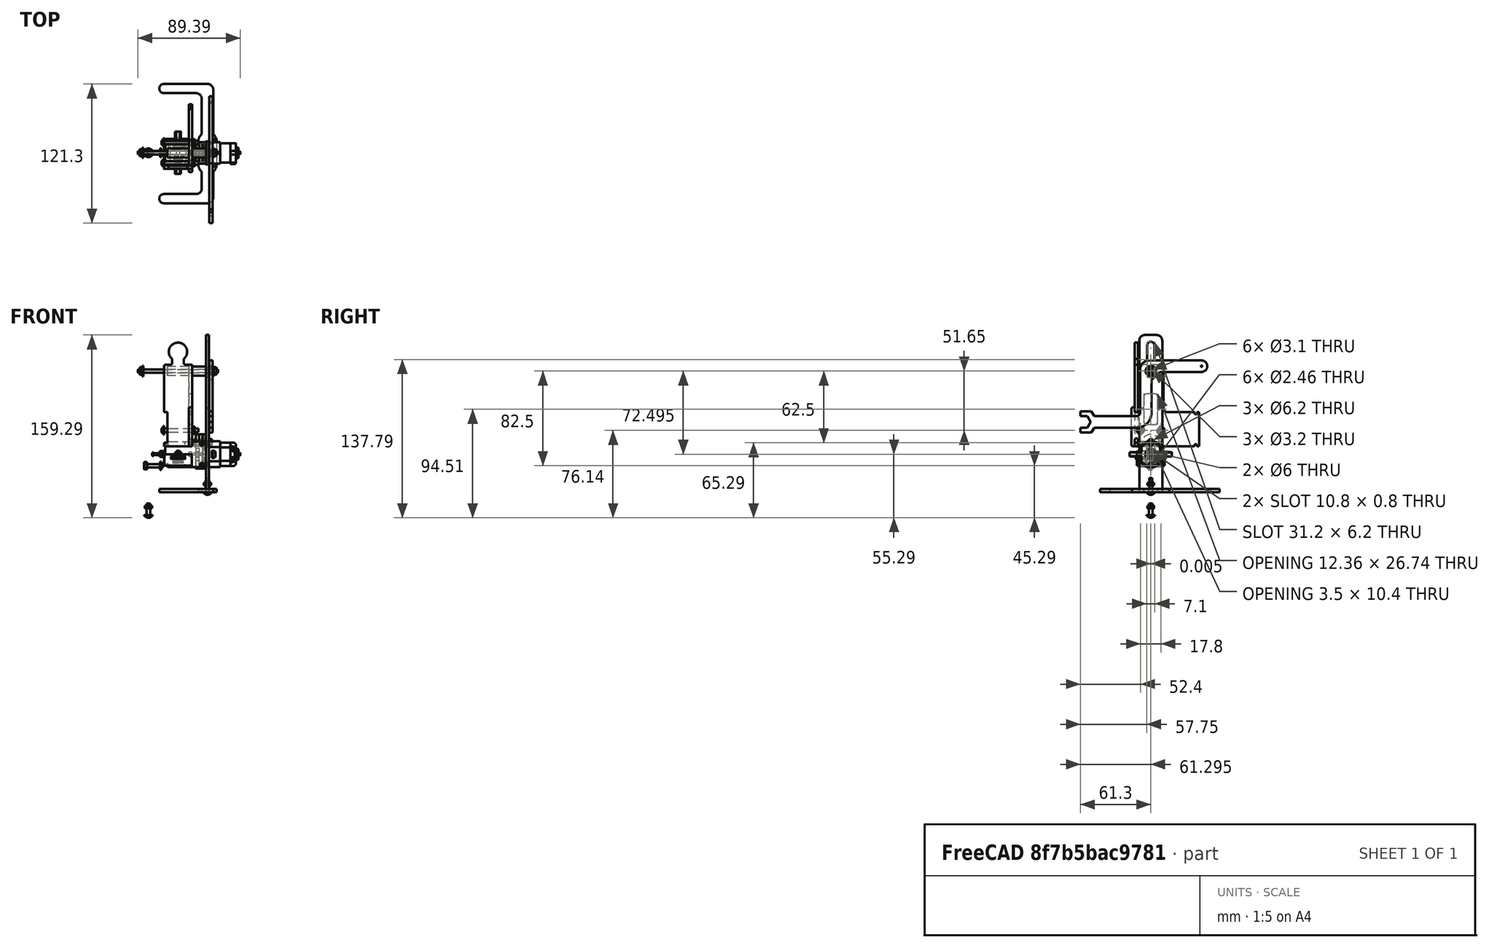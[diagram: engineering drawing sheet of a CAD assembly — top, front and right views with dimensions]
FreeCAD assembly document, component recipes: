
FREECAD ASSEMBLY — COMPONENT RECIPES ("legged_robot_06")

This assembly document has 23 components, labeled P0..P22 below (a component is one placed body or linked part). 21 of them carry a construction recipe — the FreeCAD feature program that regenerates the part from scratch, quoted from this document or its linked companion documents; the rest are supplied as boundary geometry only. No exploded tour is included for this assembly.
COMPONENT P0 — recipe-attached ("cam_right_1", modeled in this document).
Construction recipe (the document's own serialized feature program — sketch geometry with constraints, then the solid features built on it; lengths are millimeters unless a unit is written):

FEATURE [PartDesign::SubShapeBinder] Binder
  BindCopyOnChange = 0
  BindMode = 0
  ClaimChildren = false
  Context = -> Body [Binder.]
  Fuse = false
  MakeFace = true
  OffsetFill = false
  OffsetIntersection = false
  OffsetJoinType = 0
  OffsetOpenResult = false
  PartialLoad = false
  Relative = true
  Support = -> [Part001]
  _Version = 2
FEATURE [Sketcher::SketchObject] Sketch
  ExternalGeometry = -> [Binder]
  FullyConstrained = true
  MapMode = 5
  Placement = pos=(-18.4,0,0) rot=(0.57735,-0.57735,-0.57735;2.0944rad)
  Support = -> [Binder]
  expr: Constraints[38] = Spreadsheet.cam_length
  expr: Constraints[81] = Spreadsheet.angle
  sketch-geometry (37):
    g0: ArcOfCircle CenterX=3.55 CenterY=5 CenterZ=0 NormalX=0 NormalY=0 NormalZ=1 AngleXU=0 Radius=0.4 StartAngle=0 EndAngle=3.14159
    g1: ArcOfCircle CenterX=3.55 CenterY=-5 CenterZ=0 NormalX=0 NormalY=0 NormalZ=1 AngleXU=0 Radius=0.4 StartAngle=3.14159 EndAngle=6.28319
    g2: LineSegment StartX=3.15 StartY=5 StartZ=0 EndX=3.15 EndY=-5 EndZ=0
    g3: LineSegment StartX=3.95 StartY=-5 StartZ=0 EndX=3.95 EndY=5 EndZ=0
    g4: ArcOfCircle CenterX=-3.55 CenterY=5 CenterZ=0 NormalX=0 NormalY=0 NormalZ=1 AngleXU=0 Radius=0.4 StartAngle=3e-16 EndAngle=3.14159
    g5: ArcOfCircle CenterX=-3.55 CenterY=-5 CenterZ=0 NormalX=0 NormalY=0 NormalZ=1 AngleXU=0 Radius=0.4 StartAngle=3.14159 EndAngle=6.28319
    g6: LineSegment StartX=-3.15 StartY=-5 StartZ=0 EndX=-3.15 EndY=5 EndZ=0
    g7: LineSegment StartX=3.55 StartY=5 StartZ=0 EndX=3.55 EndY=-5 EndZ=0
    g8: LineSegment StartX=-3.55 StartY=5 StartZ=0 EndX=-3.55 EndY=-5 EndZ=0
    g9: ArcOfCircle CenterX=1.55 CenterY=5 CenterZ=0 NormalX=0 NormalY=0 NormalZ=1 AngleXU=0 Radius=0.2 StartAngle=0 EndAngle=3.14159
    g10: ArcOfCircle CenterX=1.55 CenterY=-5 CenterZ=0 NormalX=0 NormalY=0 NormalZ=1 AngleXU=0 Radius=0.2 StartAngle=3.14159 EndAngle=6.28319
    g11: LineSegment StartX=1.35 StartY=5 StartZ=0 EndX=1.35 EndY=2.16333 EndZ=0
    g12: LineSegment StartX=1.75 StartY=-5 StartZ=0 EndX=1.75 EndY=5 EndZ=0
    g13: ArcOfCircle CenterX=-1.55 CenterY=5 CenterZ=0 NormalX=0 NormalY=0 NormalZ=1 AngleXU=0 Radius=0.2 StartAngle=5e-16 EndAngle=3.14159
    g14: ArcOfCircle CenterX=-1.55 CenterY=-5 CenterZ=0 NormalX=0 NormalY=0 NormalZ=1 AngleXU=0 Radius=0.2 StartAngle=3.14159 EndAngle=6.28319
    g15: LineSegment StartX=-1.75 StartY=5 StartZ=0 EndX=-1.75 EndY=-5 EndZ=0
    g16: LineSegment StartX=-1.35 StartY=-5 StartZ=0 EndX=-1.35 EndY=-2.16333 EndZ=0
    g17: LineSegment StartX=1.55 StartY=5 StartZ=0 EndX=1.55 EndY=-5 EndZ=0
    g18: LineSegment StartX=-1.55 StartY=5 StartZ=0 EndX=-1.55 EndY=-5 EndZ=0
    g19: LineSegment StartX=3.55 StartY=-4.2e-15 StartZ=0 EndX=1.55 EndY=-3.8e-15 EndZ=0
    g20: ArcOfCircle CenterX=9.6e-15 CenterY=5 CenterZ=0 NormalX=0 NormalY=0 NormalZ=1 AngleXU=0 Radius=7.5 StartAngle=0 EndAngle=3.14159
    g21: ArcOfCircle CenterX=6.9e-15 CenterY=-10 CenterZ=0 NormalX=0 NormalY=0 NormalZ=1 AngleXU=0 Radius=7.5 StartAngle=3.14159 EndAngle=6.28319
    g22: LineSegment StartX=-7.5 StartY=5 StartZ=0 EndX=-7.5 EndY=-10 EndZ=0
    g23: LineSegment StartX=7.5 StartY=-10 StartZ=0 EndX=7.5 EndY=5 EndZ=0
    g24: LineSegment StartX=8.7e-15 StartY=-3.6e-15 StartZ=0 EndX=9.6e-15 EndY=5 EndZ=0
    g25: LineSegment StartX=8.7e-15 StartY=-3.6e-15 StartZ=0 EndX=6.9e-15 EndY=-10 EndZ=0
    g26: Circle CenterX=6.9e-15 CenterY=-10 CenterZ=0 NormalX=0 NormalY=0 NormalZ=1 AngleXU=0 Radius=3.1
    g27: LineSegment StartX=-3.95 StartY=-5 StartZ=0 EndX=-3.95 EndY=5 EndZ=0
    g28: LineSegment StartX=1.55 StartY=-3.8e-15 StartZ=0 EndX=8.7e-15 EndY=-3.6e-15 EndZ=0
    g29: Circle CenterX=8.7e-15 CenterY=-3.6e-15 CenterZ=0 NormalX=0 NormalY=0 NormalZ=1 AngleXU=0 Radius=1.75
    g30: LineSegment StartX=-1.75 StartY=-4.1e-15 StartZ=0 EndX=-1.85 EndY=-4.1e-15 EndZ=0
    g31: LineSegment StartX=-3.55 StartY=-2.9e-15 StartZ=0 EndX=-1.55 EndY=-3.3e-15 EndZ=0
    g32: LineSegment StartX=8.7e-15 StartY=-3.6e-15 StartZ=0 EndX=-1.55 EndY=-3.3e-15 EndZ=0
    g33: LineSegment StartX=-1.35 StartY=2.16333 StartZ=0 EndX=-1.35 EndY=5 EndZ=0
    g34: LineSegment StartX=1.35 StartY=-2.16333 StartZ=0 EndX=1.35 EndY=-5 EndZ=0
    g35: ArcOfCircle CenterX=8.7e-15 CenterY=-3.6e-15 CenterZ=0 NormalX=0 NormalY=0 NormalZ=1 AngleXU=0 Radius=2.55 StartAngle=1.01289 EndAngle=2.1287
    g36: ArcOfCircle CenterX=8.7e-15 CenterY=-3.6e-15 CenterZ=0 NormalX=0 NormalY=0 NormalZ=1 AngleXU=0 Radius=2.55 StartAngle=4.15448 EndAngle=5.2703
  constraints (89):
    c: Tangent(g0,g2) = -1.5708
    c: Tangent(g2,g1) = -1.5708
    c: Tangent(g1,g3) = -1.5708
    c: Tangent(g5,g6) = -1.5708
    c: Tangent(g6,g4) = -1.5708
    c: Radius(g0) = 0.4
    c: Coincident(g7,g0)
    c: Coincident(g7,g1)
    c: Coincident(g8,g4)
    c: Coincident(g8,g5)
    c: Equal(g7,g8)
    c: Distance(g7) = 10
    c: Tangent(g9,g11) = -1.5708
    c: Tangent(g10,g12) = -1.5708
    c: Tangent(g12,g9) = -1.5708
    c: Tangent(g13,g15) = -1.5708
    c: Tangent(g15,g14) = -1.5708
    c: Tangent(g14,g16) = -1.5708
    c: Coincident(g17,g9)
    c: Coincident(g17,g10)
    c: Coincident(g18,g13)
    c: Coincident(g18,g14)
    c: Equal(g17,g7)
    c: Equal(g8,g18)
    c: Symmetric(g10,g9,g19)
    c: Distance(g19) = 2
    c: Perpendicular(g7,g19)
    c: Parallel(g17,g7)
    c: Parallel(g18,g8)
    c: Tangent(g20,g22) = -1.5708
    c: Tangent(g22,g21) = -1.5708
    c: Tangent(g21,g23) = -1.5708
    c: Tangent(g23,g20) = -1.5708
    c: Equal(g20,g21)
    c: Coincident(g24,g20)
    c: Coincident(g25,g21)
    c: Diameter(g20) = 15
    c: Distance(g24) = 5
    c: Distance(g25) = 10
    c: Coincident(g26,g21)
    c: Diameter(g26) = 6.2
    c: Tangent(g27,g4) = 1.5708
    c: Tangent(g27,g5) = 1.5708
    c: Symmetric(g0,g1,g19)
    c: Coincident(g28,g19)
    c: Parallel(g28,g19)
    c: Perpendicular(g28,g24)
    c: Tangent(g0,g3) = -1.5708
    c: PointOnObject(g30,g29)
    c: Horizontal(g30)
    c: Symmetric(g-5,g-5,g30)
    c: DistanceX(g30,g30) = 0.1
    c: Perpendicular(g25,g28)
    c: Symmetric(g14,g13,g31)
    c: Symmetric(g5,g4,g31)
    c: Equal(g31,g19)
    c: Coincident(g32,g31)
    c: Equal(g28,g32)
    c: Perpendicular(g32,g24)
    c: Perpendicular(g32,g18)
    c: Perpendicular(g18,g31)
    c: Tangent(g15,g29)
    c: PointOnObject(g34,g11)
    c: PointOnObject(g33,g-3)
    c: Parallel(g33,g17)
    c: Parallel(g17,g34)
    c: Tangent(g33,g13) = -1.5708
    c: Tangent(g34,g10) = -1.5708
    c: Coincident(g25,g32)
    c: Coincident(g25,g24)
    c: Coincident(g25,g28)
    c: Coincident(g24,g29)
    c: Coincident(g35,g24)
    c: Coincident(g35,g33)
    c: Coincident(g35,g11)
    c: Coincident(g36,g35)
    c: Coincident(g36,g34)
    c: Equal(g36,g-4)
    c: Coincident(g16,g36)
    c: Parallel(g16,g18)
    c: Coincident(g35,g-4)
    c: Angle(g25) = 4.71239
    c: Equal(g5,g1)
    c: Equal(g1,g4)
    c: Equal(g4,g0)
    c: Equal(g13,g9)
    c: Equal(g9,g14)
    c: Equal(g14,g10)
    c: Radius(g9) = 0.2
FEATURE [PartDesign::Pad] Pad
  Direction = (-1,2e-16,-2e-16)
  Length = 2.8
  Length2 = 10
  Profile = -> Sketch
  ReferenceAxis = -> Sketch [N_Axis]
  Reversed = true
  Type = 0
  expr: Length = Spreadsheet.acrylic_thin
FEATURE [PartDesign::Body] Body  label="cam_right_1"
  Group = -> [Sketch,Binder,Pad]
  Origin = -> Origin001
  Tip = -> Pad
COMPONENT P1 — recipe-attached ("leg_right", modeled in this document).
Construction recipe (the document's own serialized feature program — sketch geometry with constraints, then the solid features built on it; lengths are millimeters unless a unit is written):

FEATURE [PartDesign::SubShapeBinder] Binder001
  BindCopyOnChange = 0
  BindMode = 0
  ClaimChildren = false
  Context = -> Body002 [Binder001.]
  Fuse = false
  MakeFace = true
  OffsetFill = false
  OffsetIntersection = false
  OffsetJoinType = 0
  OffsetOpenResult = false
  PartialLoad = false
  Relative = true
  Support = -> [Part001]
  _Version = 2
FEATURE [PartDesign::SubShapeBinder] Binder004
  BindCopyOnChange = 0
  BindMode = 0
  ClaimChildren = false
  Context = -> Body002 [Binder004.]
  Fuse = false
  MakeFace = true
  OffsetFill = false
  OffsetIntersection = false
  OffsetJoinType = 0
  OffsetOpenResult = false
  PartialLoad = false
  Relative = true
  Support = -> [Body004]
  _Version = 2
FEATURE [PartDesign::Plane] DatumPlane003
  AttachmentOffset = pos=(0,0,0.1) rot=(0,0,1;0rad)
  Length = 66.5529
  MapMode = 5
  Placement = pos=(-24.3,-2.7e-15,-2.7e-15) rot=(0.57735,-0.57735,-0.57735;2.0944rad)
  ResizeMode = 0
  Support = -> [Binder004]
  Width = 153.553
FEATURE [Sketcher::SketchObject] Sketch001
  ExternalGeometry = -> [Binder004]
  FullyConstrained = true
  MapMode = 5
  Placement = pos=(-24.3,-2.7e-15,-2.7e-15) rot=(0.57735,-0.57735,-0.57735;2.0944rad)
  Support = -> [DatumPlane003]
  expr: Constraints[117] = Spreadsheet.angle
  expr: Constraints[124] = Spreadsheet.acrylic_thin
  expr: Constraints[50] = Spreadsheet.cam_length
  sketch-geometry (45):
    g0: LineSegment StartX=-10 StartY=84 StartZ=0 EndX=10 EndY=84 EndZ=0
    g1: LineSegment StartX=10 StartY=84 StartZ=0 EndX=10 EndY=-53 EndZ=0
    g2: LineSegment StartX=10 StartY=-53 StartZ=0 EndX=-10 EndY=-53 EndZ=0
    g3: LineSegment StartX=-10 StartY=-53 StartZ=0 EndX=-10 EndY=84 EndZ=0
    g4: LineSegment StartX=1.6 StartY=-9.07624 StartZ=0 EndX=-3.1e-15 EndY=-8.15248 EndZ=0
    g5: LineSegment StartX=-3.1e-15 StartY=-8.15248 StartZ=0 EndX=-1.6 EndY=-9.07624 EndZ=0
    g6: LineSegment StartX=-1.6 StartY=-9.07624 StartZ=0 EndX=-1.6 EndY=-10.9238 EndZ=0
    g7: LineSegment StartX=-1.6 StartY=-10.9238 StartZ=0 EndX=-4.4e-15 EndY=-11.8475 EndZ=0
    g8: LineSegment StartX=-4.4e-15 StartY=-11.8475 StartZ=0 EndX=1.6 EndY=-10.9238 EndZ=0
    g9: LineSegment StartX=1.6 StartY=-10.9238 StartZ=0 EndX=1.6 EndY=-9.07624 EndZ=0
    g10: Circle CenterX=-1.8e-15 CenterY=-10 CenterZ=0 NormalX=0 NormalY=0 NormalZ=1 AngleXU=0 Radius=1.84752
    g11: LineSegment StartX=-1.8e-15 StartY=-10 StartZ=0 EndX=-10 EndY=-10 EndZ=0
    g12: LineSegment StartX=-1.8e-15 StartY=-10 StartZ=0 EndX=10 EndY=-10 EndZ=0
    g13: ArcOfCircle CenterX=8e-16 CenterY=75 CenterZ=0 NormalX=0 NormalY=0 NormalZ=1 AngleXU=0 Radius=3.1 StartAngle=-2.7e-15 EndAngle=3.14159
    g14: ArcOfCircle CenterX=-2e-16 CenterY=50 CenterZ=0 NormalX=0 NormalY=0 NormalZ=1 AngleXU=0 Radius=3.1 StartAngle=3.14159 EndAngle=6.28319
    g15: LineSegment StartX=-3.1 StartY=75 StartZ=0 EndX=-3.1 EndY=50 EndZ=0
    g16: LineSegment StartX=3.1 StartY=50 StartZ=0 EndX=3.1 EndY=75 EndZ=0
    g17: LineSegment StartX=8e-16 StartY=75 StartZ=0 EndX=1.2e-15 EndY=84 EndZ=0
    g18: Circle CenterX=-1.8e-15 CenterY=-10 CenterZ=0 NormalX=0 NormalY=0 NormalZ=1 AngleXU=0 Radius=1.6
    g19: LineSegment StartX=0 StartY=0 StartZ=0 EndX=-1.8e-15 EndY=-10 EndZ=0
    g20: Circle CenterX=0 CenterY=71 CenterZ=0 NormalX=0 NormalY=0 NormalZ=1 AngleXU=0 Radius=3.1
    g21: LineSegment StartX=0 StartY=71 StartZ=0 EndX=0 EndY=0 EndZ=0
    g22: LineSegment StartX=-2e-16 StartY=50 StartZ=0 EndX=3e-16 EndY=62.5 EndZ=0
    g23: LineSegment StartX=8e-16 StartY=75 StartZ=0 EndX=3e-16 EndY=62.5 EndZ=0
    g24: LineSegment StartX=-10 StartY=-53 StartZ=0 EndX=-6 EndY=-53 EndZ=0
    g25: LineSegment StartX=-6 StartY=-53 StartZ=0 EndX=-6 EndY=-50.2 EndZ=0
    g26: LineSegment StartX=-6 StartY=-50.2 StartZ=0 EndX=-1.25 EndY=-50.2 EndZ=0
    g27: LineSegment StartX=-1.25 StartY=-50.2 StartZ=0 EndX=-1.25 EndY=-47.2 EndZ=0
    g28: LineSegment StartX=-1.25 StartY=-47.2 StartZ=0 EndX=-2.75 EndY=-47.2 EndZ=0
    g29: LineSegment StartX=-2.75 StartY=-47.2 StartZ=0 EndX=-2.75 EndY=-44.7 EndZ=0
    g30: LineSegment StartX=-2.75 StartY=-44.7 StartZ=0 EndX=-1.25 EndY=-44.7 EndZ=0
    g31: LineSegment StartX=-1.25 StartY=-44.7 StartZ=0 EndX=-1.25 EndY=-40.7 EndZ=0
    g32: LineSegment StartX=-1.25 StartY=-40.7 StartZ=0 EndX=1.25 EndY=-40.7 EndZ=0
    g33: LineSegment StartX=1.25 StartY=-40.7 StartZ=0 EndX=1.25 EndY=-44.7 EndZ=0
    g34: LineSegment StartX=1.25 StartY=-44.7 StartZ=0 EndX=2.75 EndY=-44.7 EndZ=0
    g35: LineSegment StartX=2.75 StartY=-44.7 StartZ=0 EndX=2.75 EndY=-47.2 EndZ=0
    g36: LineSegment StartX=2.75 StartY=-47.2 StartZ=0 EndX=1.25 EndY=-47.2 EndZ=0
    g37: LineSegment StartX=1.25 StartY=-47.2 StartZ=0 EndX=1.25 EndY=-50.2 EndZ=0
    g38: LineSegment StartX=1.25 StartY=-50.2 StartZ=0 EndX=6 EndY=-50.2 EndZ=0
    g39: LineSegment StartX=6 StartY=-50.2 StartZ=0 EndX=6 EndY=-53 EndZ=0
    g40: LineSegment StartX=6 StartY=-53 StartZ=0 EndX=10 EndY=-53 EndZ=0
    g41: LineSegment StartX=-7 StartY=-10 StartZ=0 EndX=-7 EndY=20 EndZ=0
    g42: LineSegment StartX=7 StartY=20 StartZ=0 EndX=7 EndY=-10 EndZ=0
    g43: Circle CenterX=-7 CenterY=20 CenterZ=0 NormalX=0 NormalY=0 NormalZ=1 AngleXU=0 Radius=0.6
    g44: Circle CenterX=7 CenterY=20 CenterZ=0 NormalX=0 NormalY=0 NormalZ=1 AngleXU=0 Radius=0.6
  constraints (123):
    c: Coincident(g0,g1)
    c: Coincident(g1,g2)
    c: Coincident(g2,g3)
    c: Coincident(g3,g0)
    c: Coincident(g4,g5)
    c: Coincident(g5,g6)
    c: Coincident(g6,g7)
    c: Coincident(g7,g8)
    c: Coincident(g8,g9)
    c: Coincident(g9,g4)
    c: Equal(g4, g5-g9) x5
    c: PointOnObject(g4,g10)
    c: PointOnObject(g5,g10)
    c: PointOnObject(g6,g10)
    c: PointOnObject(g7,g10)
    c: PointOnObject(g8,g10)
    c: PointOnObject(g9,g10)
    c: Distance(g0) = 20
    c: Perpendicular(g3,g0)
    c: Perpendicular(g1,g2)
    c: Perpendicular(g2,g3)
    c: Coincident(g11,g10)
    c: PointOnObject(g11,g3)
    c: Coincident(g12,g10)
    c: PointOnObject(g12,g1)
    c: Perpendicular(g1,g12)
    c: Perpendicular(g3,g11)
    c: Equal(g11,g12)
    c: Distance(g3) = 137
    c: Perpendicular(g11,g6)
    c: Tangent(g13,g15) = -1.5708
    c: Tangent(g15,g14) = -1.5708
    c: Tangent(g14,g16) = -1.5708
    c: Tangent(g16,g13) = -1.5708
    c: Equal(g13,g14)
    c: Diameter(g14) = 6.2
    c: Distance(g13,g14) = 25
    c: Coincident(g17,g13)
    c: Perpendicular(g0,g17)
    c: Distance(g17) = 9
    c: Distance(g10,g14) = 60
    c: Symmetric(g0,g0,g17)
    c: Parallel(g15,g3)
    c: Coincident(g18,g10)
    c: Diameter(g18) = 3.2
    c: Coincident(g19,g10)
    c: Distance(g19) = 10
    c: Coincident(g21,g20)
    c: DistanceY(g21,g21) = 71
    c: Coincident(g21,g19)
    c: Coincident(g22,g14)
    c: Coincident(g23,g13)
    c: Coincident(g23,g22)
    c: Equal(g23,g22)
    c: Parallel(g23,g15)
    c: Tangent(g20,g16)
    c: Vertical(g21)
    c: Coincident(g24,g3)
    c: Coincident(g24,g25)
    c: Coincident(g25,g26)
    c: Coincident(g26,g27)
    c: Coincident(g27,g28)
    c: Coincident(g28,g29)
    c: Coincident(g29,g30)
    c: Coincident(g30,g31)
    c: Coincident(g31,g32)
    c: Coincident(g32,g33)
    c: Coincident(g33,g34)
    c: Coincident(g34,g35)
    c: Coincident(g35,g36)
    c: Coincident(g36,g37)
    c: Coincident(g37,g38)
    c: Coincident(g38,g39)
    c: Coincident(g39,g40)
    c: Coincident(g40,g1)
    c: Perpendicular(g24,g3)
    c: Perpendicular(g40,g1)
    c: Perpendicular(g39,g40)
    c: Perpendicular(g24,g25)
    c: Perpendicular(g26,g25)
    c: Perpendicular(g39,g38)
    c: Perpendicular(g38,g37)
    c: Perpendicular(g26,g27)
    c: Perpendicular(g36,g37)
    c: Perpendicular(g27,g28)
    c: Perpendicular(g35,g36)
    c: Perpendicular(g29,g28)
    c: Perpendicular(g35,g34)
    c: Perpendicular(g30,g29)
    c: Perpendicular(g34,g33)
    c: Perpendicular(g31,g30)
    c: Equal(g25,g39)
    c: Equal(g37,g27)
    c: Equal(g36,g28)
    c: Equal(g30,g34)
    c: Equal(g26,g38)
    c: Distance(g29,g34) = 5.5
    c: Equal(g32,g29)
    c: Equal(g29,g35)
    c: Distance(g31) = 4
    c: Perpendicular(g32,g33)
    c: Equal(g28,g30)
    c: PointOnObject(g41,g11)
    c: Symmetric(g41,g42,g10)
    c: Equal(g41,g42)
    c: Distance(g41,g11) = 3
    c: Coincident(g43,g41)
    c: Coincident(g44,g42)
    c: Equal(g44,g43)
    c: Diameter(g44) = 1.2
    c: Distance(g41) = 30
    c: Perpendicular(g12,g42)
    c: Perpendicular(g11,g41)
    c: Angle(g19) = 4.71239
    c: Equal(g24,g40)
    c: Distance(g24) = 4
    c: DistanceY(g3,g19) = 53
    c: Tangent(g18,g6)
    c: Coincident(g19,g-1)
    c: DistanceY(g29,g29) = 2.5
    c: DistanceY(g25,g25) = 2.8
    c: DistanceY(g27,g27) = 3
    c: Equal(g14,g20)
FEATURE [PartDesign::Pad] Pad004
  Direction = (-1,1e-16,-3e-16)
  Length = 2.8
  Length2 = 10
  Placement = pos=(-24.3,-3e-15,-5e-15) rot=(0.57735,-0.57735,-0.57735;2.0944rad)
  Profile = -> Sketch001
  ReferenceAxis = -> Sketch001 [N_Axis]
  Type = 0
  expr: Length = Spreadsheet.acrylic_thin
FEATURE [PartDesign::Fillet] Fillet
  Base = -> Pad004 [Edge1,Edge2,Edge11,Edge14,Edge53,Edge20,Edge38,Edge35,Edge50,Edge23,Edge41,Edge32,Edge26,Edge47,Edge44,Edge29]
  BaseFeature = -> Pad004
  Placement = pos=(-24.3,-3e-15,-5e-15) rot=(0.57735,-0.57735,-0.57735;2.0944rad)
  Radius = 0.4
  SupportTransform = false
  UseAllEdges = false
FEATURE [PartDesign::Fillet] Fillet001
  Base = -> Fillet [Edge101,Edge103]
  BaseFeature = -> Fillet
  Placement = pos=(-24.3,-3e-15,-5e-15) rot=(0.57735,-0.57735,-0.57735;2.0944rad)
  Radius = 5
  SupportTransform = false
  UseAllEdges = false
FEATURE [PartDesign::Body] Body002  label="leg_right"
  Group = -> [Sketch001,Binder001,Binder004,DatumPlane003,Pad004,Fillet,Fillet001]
  Origin = -> Origin003
  Tip = -> Fillet001
COMPONENT P2 — recipe-attached ("cam_right_2", modeled in this document).
Construction recipe (the document's own serialized feature program — sketch geometry with constraints, then the solid features built on it; lengths are millimeters unless a unit is written):

FEATURE [PartDesign::SubShapeBinder] Binder002
  BindCopyOnChange = 0
  BindMode = 0
  ClaimChildren = false
  Context = -> Body003 [Binder002.]
  Fuse = false
  MakeFace = true
  OffsetFill = false
  OffsetIntersection = false
  OffsetJoinType = 0
  OffsetOpenResult = false
  PartialLoad = false
  Relative = true
  Support = -> [Body]
  _Version = 2
FEATURE [PartDesign::Plane] DatumPlane001
  AttachmentOffset = pos=(0,0,0.1) rot=(0,0,1;0rad)
  Length = 60
  MapMode = 5
  Placement = pos=(-18.5,5.2e-15,-3.9e-15) rot=(-0.57735,0.57735,0.57735;4.18879rad)
  ResizeMode = 0
  Support = -> [Binder002]
  Width = 60
FEATURE [Sketcher::SketchObject] Sketch002
  ExternalGeometry = -> [Binder002]
  FullyConstrained = true
  MapMode = 5
  Placement = pos=(-18.5,5.2e-15,-3.9e-15) rot=(-0.57735,0.57735,0.57735;4.18879rad)
  Support = -> [DatumPlane001]
  sketch-geometry (6):
    g0: ArcOfCircle CenterX=-1.6948e-12 CenterY=5 CenterZ=0 NormalX=0 NormalY=0 NormalZ=1 AngleXU=0 Radius=7.5 StartAngle=2.58e-13 EndAngle=3.14159
    g1: ArcOfCircle CenterX=2.174e-12 CenterY=-10 CenterZ=0 NormalX=0 NormalY=0 NormalZ=1 AngleXU=0 Radius=7.5 StartAngle=3.14159 EndAngle=6.28319
    g2: LineSegment StartX=-7.5 StartY=5 StartZ=0 EndX=-7.5 EndY=-10 EndZ=0
    g3: LineSegment StartX=7.5 StartY=-10 StartZ=0 EndX=7.5 EndY=5 EndZ=0
    g4: Circle CenterX=2.174e-12 CenterY=-10 CenterZ=0 NormalX=0 NormalY=0 NormalZ=1 AngleXU=0 Radius=3.1
    g5: Circle CenterX=0 CenterY=0 CenterZ=0 NormalX=0 NormalY=0 NormalZ=1 AngleXU=0 Radius=1
  constraints (12):
    c: Tangent(g0,g2) = -1.5708
    c: Tangent(g2,g1) = -1.5708
    c: Tangent(g1,g3) = -1.5708
    c: Tangent(g3,g0) = -1.5708
    c: Equal(g0,g1)
    c: Coincident(g0,g-3)
    c: Coincident(g1,g-5)
    c: Equal(g0,g-3)
    c: Coincident(g4,g1)
    c: Equal(g4,g-5)
    c: Coincident(g5,g-6)
    c: Diameter(g5) = 2
FEATURE [PartDesign::Pad] Pad002
  Direction = (-1,2e-16,-2e-16)
  Length = 2.8
  Length2 = 10
  Placement = pos=(-18.5,5e-15,-4e-15) rot=(0.57735,-0.57735,-0.57735;2.0944rad)
  Profile = -> Sketch002
  ReferenceAxis = -> Sketch002 [N_Axis]
  Type = 0
  expr: Length = Spreadsheet.acrylic_thin
FEATURE [PartDesign::Body] Body003  label="cam_right_2"
  Group = -> [Binder002,DatumPlane001,Sketch002,Pad002]
  Origin = -> Origin
  Tip = -> Pad002
COMPONENT P3 — recipe-attached ("cam_right_3", modeled in this document).
Construction recipe (the document's own serialized feature program — sketch geometry with constraints, then the solid features built on it; lengths are millimeters unless a unit is written):

FEATURE [PartDesign::SubShapeBinder] Binder003
  BindCopyOnChange = 0
  BindMode = 0
  ClaimChildren = false
  Context = -> Body004 [Binder003.]
  Fuse = false
  MakeFace = true
  OffsetFill = false
  OffsetIntersection = false
  OffsetJoinType = 0
  OffsetOpenResult = false
  PartialLoad = false
  Relative = true
  Support = -> [Body003]
  _Version = 2
FEATURE [PartDesign::Plane] DatumPlane002
  AttachmentOffset = pos=(0,0,0.1) rot=(0,0,1;0rad)
  Length = 60
  MapMode = 5
  Placement = pos=(-21.4,5.3e-15,-1.05e-14) rot=(-0.57735,0.57735,0.57735;4.18879rad)
  ResizeMode = 0
  Support = -> [Binder003]
  Width = 60
FEATURE [Sketcher::SketchObject] Sketch003
  ExternalGeometry = -> [Binder003]
  FullyConstrained = true
  MapMode = 5
  Placement = pos=(-21.4,5.3e-15,-1.05e-14) rot=(-0.57735,0.57735,0.57735;4.18879rad)
  Support = -> [DatumPlane002]
  sketch-geometry (6):
    g0: ArcOfCircle CenterX=-1.6956e-12 CenterY=5 CenterZ=0 NormalX=0 NormalY=0 NormalZ=1 AngleXU=0 Radius=7.5 StartAngle=2.581e-13 EndAngle=3.14159
    g1: ArcOfCircle CenterX=2.1765e-12 CenterY=-10 CenterZ=0 NormalX=0 NormalY=0 NormalZ=1 AngleXU=0 Radius=7.5 StartAngle=3.14159 EndAngle=6.28319
    g2: LineSegment StartX=-7.5 StartY=5 StartZ=0 EndX=-7.5 EndY=-10 EndZ=0
    g3: LineSegment StartX=7.5 StartY=-10 StartZ=0 EndX=7.5 EndY=5 EndZ=0
    g4: Circle CenterX=2.1765e-12 CenterY=-10 CenterZ=0 NormalX=0 NormalY=0 NormalZ=1 AngleXU=0 Radius=3.1
    g5: Circle CenterX=0 CenterY=0 CenterZ=0 NormalX=0 NormalY=0 NormalZ=1 AngleXU=0 Radius=3
  constraints (12):
    c: Tangent(g0,g2) = -1.5708
    c: Tangent(g2,g1) = -1.5708
    c: Tangent(g1,g3) = -1.5708
    c: Tangent(g3,g0) = -1.5708
    c: Equal(g0,g1)
    c: Coincident(g0,g-3)
    c: Coincident(g1,g-5)
    c: Equal(g0,g-3)
    c: Coincident(g4,g1)
    c: Equal(g4,g-5)
    c: Coincident(g5,g-6)
    c: Diameter(g5) = 6
FEATURE [PartDesign::Pad] Pad003
  Direction = (-1,0,0)
  Length = 2.8
  Length2 = 10
  Placement = pos=(-21.4,1e-15,-2e-15) rot=(0.57735,-0.57735,-0.57735;2.0944rad)
  Profile = -> Sketch003
  ReferenceAxis = -> Sketch003 [N_Axis]
  Type = 0
  expr: Length = Spreadsheet.acrylic_thin
FEATURE [PartDesign::Body] Body004  label="cam_right_3"
  Group = -> [Binder003,DatumPlane002,Sketch003,Pad003]
  Origin = -> Origin005
  Tip = -> Pad003
COMPONENT P4 — recipe-attached ("spacer_right", modeled in this document).
Construction recipe (the document's own serialized feature program — sketch geometry with constraints, then the solid features built on it; lengths are millimeters unless a unit is written):

FEATURE [PartDesign::SubShapeBinder] Binder005
  BindCopyOnChange = 0
  BindMode = 0
  ClaimChildren = false
  Context = -> Body005 [Binder005.]
  Fuse = false
  MakeFace = true
  OffsetFill = false
  OffsetIntersection = false
  OffsetJoinType = 0
  OffsetOpenResult = false
  PartialLoad = false
  Relative = true
  Support = -> [Body004]
  _Version = 2
FEATURE [PartDesign::SubShapeBinder] Binder008
  BindCopyOnChange = 0
  BindMode = 0
  ClaimChildren = false
  Context = -> Body005 [Binder008.]
  Fuse = false
  MakeFace = true
  OffsetFill = false
  OffsetIntersection = false
  OffsetJoinType = 0
  OffsetOpenResult = false
  PartialLoad = false
  Relative = true
  Support = -> [Body002[Pad004.]]
  _Version = 2
FEATURE [Sketcher::SketchObject] Sketch004
  ExternalGeometry = -> [Binder005]
  FullyConstrained = true
  MapMode = 5
  Placement = pos=(-24.3,6.3e-15,-8e-15) rot=(0.57735,0.57735,0.57735;2.0944rad)
  Support = -> [Binder008]
  sketch-geometry (2):
    g0: Circle CenterX=-2.1858e-12 CenterY=-10 CenterZ=0 NormalX=0 NormalY=0 NormalZ=1 AngleXU=0 Radius=3
    g1: Circle CenterX=-2.1858e-12 CenterY=-10 CenterZ=0 NormalX=0 NormalY=0 NormalZ=1 AngleXU=0 Radius=1.6
  constraints (4):
    c: Diameter(g1) = 3.2
    c: Diameter(g0) = 6
    c: Coincident(g1,g-3)
    c: Coincident(g0,g1)
FEATURE [PartDesign::Pad] Pad005
  Direction = (1,-1e-16,4e-16)
  Length = 8.8
  Length2 = 10
  Profile = -> Sketch004
  ReferenceAxis = -> Sketch004 [N_Axis]
  Type = 0
FEATURE [PartDesign::Body] Body005  label="spacer_right"
  Group = -> [Binder005,Sketch004,Pad005,Binder008]
  Origin = -> Origin006
  Tip = -> Pad005
COMPONENT P5 — recipe-attached ("feet_right", modeled in this document).
Construction recipe (the document's own serialized feature program — sketch geometry with constraints, then the solid features built on it; lengths are millimeters unless a unit is written):

FEATURE [PartDesign::SubShapeBinder] Binder009
  BindCopyOnChange = 0
  BindMode = 0
  ClaimChildren = false
  Context = -> Body007 [Binder009.]
  Fuse = false
  MakeFace = true
  OffsetFill = false
  OffsetIntersection = false
  OffsetJoinType = 0
  OffsetOpenResult = false
  PartialLoad = false
  Relative = true
  Support = -> [Body002[Pad004.]]
  _Version = 2
FEATURE [PartDesign::Plane] DatumPlane
  Length = 74.3266
  MapMode = 5
  Placement = pos=(-5.8e-15,-1.75e-14,-53) rot=(1,0,0;3.14159rad)
  ResizeMode = 0
  Support = -> [Binder009]
  Width = 119.627
FEATURE [Sketcher::SketchObject] Sketch006
  ExternalGeometry = -> [Binder009]
  FullyConstrained = true
  MapMode = 5
  Placement = pos=(-5.8e-15,-1.75e-14,-53) rot=(0,0,1;3.14159rad)
  Support = -> [DatumPlane]
  sketch-geometry (51):
    g0: LineSegment StartX=-12.3 StartY=40 StartZ=0 EndX=25.7 EndY=40 EndZ=0
    g1: LineSegment StartX=25.7 StartY=40 StartZ=0 EndX=25.7 EndY=0 EndZ=0
    g2: LineSegment StartX=25.7 StartY=0 StartZ=0 EndX=25.7 EndY=-56 EndZ=0
    g3: LineSegment StartX=25.7 StartY=-56 StartZ=0 EndX=-12.3 EndY=-56 EndZ=0
    g4: ArcOfCircle CenterX=-12.3 CenterY=40 CenterZ=0 NormalX=0 NormalY=0 NormalZ=1 AngleXU=0 Radius=4 StartAngle=1.5708 EndAngle=4.71239
    g5: ArcOfCircle CenterX=-12.3 CenterY=-56 CenterZ=0 NormalX=0 NormalY=0 NormalZ=1 AngleXU=0 Radius=4 StartAngle=1.5708 EndAngle=4.71239
    g6: LineSegment StartX=-12.3 StartY=44 StartZ=0 EndX=25.7 EndY=44 EndZ=0
    g7: LineSegment StartX=-12.3 StartY=36 StartZ=0 EndX=15.7 EndY=36 EndZ=0
    g8: LineSegment StartX=-12.3 StartY=-52 StartZ=0 EndX=15.7 EndY=-52 EndZ=0
    g9: LineSegment StartX=-12.3 StartY=-60 StartZ=0 EndX=25.7 EndY=-60 EndZ=0
    g10: ArcOfCircle CenterX=25.7 CenterY=10.1 CenterZ=0 NormalX=0 NormalY=0 NormalZ=1 AngleXU=0 Radius=8 StartAngle=0 EndAngle=0.895665
    g11: ArcOfCircle CenterX=25.7 CenterY=-9.9 CenterZ=0 NormalX=0 NormalY=0 NormalZ=1 AngleXU=0 Radius=8 StartAngle=3.14159 EndAngle=4.03726
    g12: LineSegment StartX=17.7 StartY=10.1 StartZ=0 EndX=17.7 EndY=-9.9 EndZ=0
    g13: LineSegment StartX=33.7 StartY=-9.9 StartZ=0 EndX=33.7 EndY=10.1 EndZ=0
    g14: LineSegment StartX=20.7 StartY=31 StartZ=0 EndX=20.7 EndY=16.345 EndZ=0
    g15: LineSegment StartX=30.7 StartY=16.345 StartZ=0 EndX=30.7 EndY=39 EndZ=0
    g16: ArcOfCircle CenterX=25.7 CenterY=39 CenterZ=0 NormalX=0 NormalY=0 NormalZ=1 AngleXU=0 Radius=5 StartAngle=0 EndAngle=1.5708
    g17: LineSegment StartX=20.7 StartY=-47 StartZ=0 EndX=20.7 EndY=-16.145 EndZ=0
    g18: LineSegment StartX=30.7 StartY=-16.145 StartZ=0 EndX=30.7 EndY=-55 EndZ=0
    g19: ArcOfCircle CenterX=25.7 CenterY=-55 CenterZ=0 NormalX=0 NormalY=0 NormalZ=1 AngleXU=0 Radius=5 StartAngle=4.71239 EndAngle=6.28319
    g20: ArcOfCircle CenterX=25.7 CenterY=-9.9 CenterZ=0 NormalX=0 NormalY=0 NormalZ=1 AngleXU=0 Radius=8 StartAngle=5.38752 EndAngle=6.28319
    g21: ArcOfCircle CenterX=25.7 CenterY=10.1 CenterZ=0 NormalX=0 NormalY=0 NormalZ=1 AngleXU=0 Radius=8 StartAngle=2.24593 EndAngle=3.14159
    g22: Circle CenterX=25.7 CenterY=0 CenterZ=0 NormalX=0 NormalY=0 NormalZ=1 AngleXU=0 Radius=1.55
    g23: LineSegment StartX=24.2 StartY=10.1 StartZ=0 EndX=27.2 EndY=10.1 EndZ=0
    g24: LineSegment StartX=27.2 StartY=10.1 StartZ=0 EndX=27.2 EndY=6.1 EndZ=0
    g25: LineSegment StartX=27.2 StartY=6.1 StartZ=0 EndX=24.2 EndY=6.1 EndZ=0
    g26: LineSegment StartX=24.2 StartY=6.1 StartZ=0 EndX=24.2 EndY=10.1 EndZ=0
    g27: LineSegment StartX=24.3 StartY=10 StartZ=0 EndX=24.3 EndY=10.1 EndZ=0
    g28: LineSegment StartX=24.3 StartY=10 StartZ=0 EndX=24.2 EndY=10 EndZ=0
    g29: LineSegment StartX=27.1 StartY=6 StartZ=0 EndX=27.2 EndY=6 EndZ=0
    g30: LineSegment StartX=27.1 StartY=6 StartZ=0 EndX=27.1 EndY=6.1 EndZ=0
    g31: LineSegment StartX=24.2 StartY=-5.9 StartZ=0 EndX=27.2 EndY=-5.9 EndZ=0
    g32: LineSegment StartX=27.2 StartY=-5.9 StartZ=0 EndX=27.2 EndY=-9.9 EndZ=0
    g33: LineSegment StartX=27.2 StartY=-9.9 StartZ=0 EndX=24.2 EndY=-9.9 EndZ=0
    g34: LineSegment StartX=24.2 StartY=-9.9 StartZ=0 EndX=24.2 EndY=-5.9 EndZ=0
    g35: LineSegment StartX=24.3 StartY=-6 StartZ=0 EndX=24.3 EndY=-5.9 EndZ=0
    g36: LineSegment StartX=24.3 StartY=-6 StartZ=0 EndX=24.2 EndY=-6 EndZ=0
    g37: LineSegment StartX=27.1 StartY=-10 StartZ=0 EndX=27.2 EndY=-10 EndZ=0
    g38: LineSegment StartX=27.1 StartY=-10 StartZ=0 EndX=27.1 EndY=-9.9 EndZ=0
    g39: ArcOfCircle CenterX=15.7 CenterY=-47 CenterZ=0 NormalX=0 NormalY=0 NormalZ=1 AngleXU=0 Radius=5 StartAngle=4.71239 EndAngle=6.28319
    g40: GeomPoint X=20.7 Y=-52 Z=0
    g41: ArcOfCircle CenterX=15.7 CenterY=31 CenterZ=0 NormalX=0 NormalY=0 NormalZ=1 AngleXU=0 Radius=5 StartAngle=0 EndAngle=1.5708
    g42: GeomPoint X=20.7 Y=36 Z=0
    g43: LineSegment StartX=24.2 StartY=10.1 StartZ=0 EndX=17.7 EndY=10.1 EndZ=0
    g44: LineSegment StartX=27.2 StartY=10.1 StartZ=0 EndX=33.7 EndY=10.1 EndZ=0
    g45: LineSegment StartX=24.2 StartY=-9.9 StartZ=0 EndX=17.7 EndY=-9.9 EndZ=0
    g46: LineSegment StartX=27.2 StartY=-9.9 StartZ=0 EndX=33.7 EndY=-9.9 EndZ=0
    g47: LineSegment StartX=24.3 StartY=1.25 StartZ=0 EndX=24.3 EndY=-1.25 EndZ=0
    g48: LineSegment StartX=27.1 StartY=1.25 StartZ=0 EndX=27.1 EndY=-1.25 EndZ=0
    g49: LineSegment StartX=24.3 StartY=1e-15 StartZ=0 EndX=25.7 EndY=0 EndZ=0
    g50: LineSegment StartX=25.7 StartY=0 StartZ=0 EndX=27.1 EndY=1e-15 EndZ=0
  constraints (133):
    c: Horizontal(g0)
    c: Coincident(g0,g1)
    c: Vertical(g1)
    c: Coincident(g1,g2)
    c: Vertical(g2)
    c: Coincident(g2,g3)
    c: Horizontal(g3)
    c: DistanceY(g2,g2) = 56
    c: Equal(g3,g0)
    c: DistanceX(g0,g0) = 38
    c: Coincident(g4,g0)
    c: Coincident(g5,g3)
    c: Equal(g5,g4)
    c: Diameter(g5) = 8
    c: Horizontal(g6)
    c: Horizontal(g7)
    c: Tangent(g4,g6) = 1.5708
    c: Tangent(g4,g7) = -1.5708
    c: Distance(g42,g1) = 5
    c: Horizontal(g8)
    c: Horizontal(g9)
    c: Tangent(g5,g8) = 1.5708
    c: Tangent(g5,g9) = -1.5708
    c: Equal(g6,g9)
    c: Tangent(g12,g11) = -1.5708
    c: Tangent(g13,g10) = -1.5708
    c: Equal(g10,g11)
    c: Diameter(g10) = 16
    c: Vertical(g14)
    c: PointOnObject(g6,g1)
    c: Vertical(g15)
    c: Tangent(g15,g16) = -1.5708
    c: Tangent(g16,g6) = 1.5708
    c: Distance(g15,g1) = 5
    c: Vertical(g17)
    c: Vertical(g18)
    c: Distance(g18,g2) = 5
    c: Tangent(g19,g9) = -1.5708
    c: Tangent(g19,g18) = 1.5708
    c: Equal(g11,g20)
    c: Coincident(g11,g17)
    c: Coincident(g20,g18)
    c: Coincident(g11,g20)
    c: Tangent(g20,g13) = -1.5708
    c: Equal(g10,g21)
    c: Coincident(g21,g14)
    c: Coincident(g10,g21)
    c: Coincident(g10,g15)
    c: Tangent(g21,g12) = -1.5708
    c: Coincident(g22,g1)
    c: Diameter(g22) = 3.1
    c: Coincident(g23,g24)
    c: Coincident(g24,g25)
    c: Coincident(g25,g26)
    c: Coincident(g26,g23)
    c: Coincident(g28,g27)
    c: Coincident(g30,g29)
    c: Equal(g28,g27)
    c: Equal(g27,g30)
    c: Equal(g30,g29)
    c: Coincident(g31,g32)
    c: Coincident(g32,g33)
    c: Coincident(g33,g34)
    c: Coincident(g34,g31)
    c: Coincident(g36,g35)
    c: Coincident(g38,g37)
    c: Coincident(g37,g-5)
    c: Coincident(g35,g-6)
    c: Coincident(g-4,g29)
    c: Coincident(g27,g-3)
    c: PointOnObject(g40,g8)
    c: PointOnObject(g40,g17)
    c: Tangent(g8,g39) = -1.5708
    c: Tangent(g17,g39) = -1.5708
    c: Radius(g39) = 5
    c: Symmetric(g11,g18,g2)
    c: PointOnObject(g42,g7)
    c: PointOnObject(g42,g14)
    c: Tangent(g7,g41) = 1.5708
    c: Tangent(g14,g41) = 1.5708
    c: Equal(g41,g39)
    c: DistanceY(g1,g1) = 40
    c: Distance(g27) = 0.1
    c: Perpendicular(g-3,g27)
    c: Perpendicular(g28,g27)
    c: PointOnObject(g28,g26)
    c: PointOnObject(g27,g23)
    c: Perpendicular(g28,g26)
    c: Perpendicular(g23,g27)
    c: Perpendicular(g-4,g30)
    c: Perpendicular(g29,g30)
    c: PointOnObject(g29,g24)
    c: PointOnObject(g30,g25)
    c: Perpendicular(g25,g30)
    c: Perpendicular(g29,g24)
    c: Perpendicular(g-5,g38)
    c: Perpendicular(g37,g38)
    c: Perpendicular(g35,g-6)
    c: Perpendicular(g36,g35)
    c: Equal(g35,g36)
    c: Equal(g36,g37)
    c: Equal(g37,g38)
    c: Equal(g38,g27)
    c: PointOnObject(g35,g31)
    c: PointOnObject(g36,g34)
    c: Perpendicular(g34,g36)
    c: Perpendicular(g31,g35)
    c: PointOnObject(g38,g33)
    c: PointOnObject(g37,g32)
    c: Perpendicular(g32,g37)
    c: Perpendicular(g33,g38)
    c: Coincident(g43,g23)
    c: Coincident(g43,g12)
    c: Coincident(g44,g23)
    c: Coincident(g44,g10)
    c: Perpendicular(g44,g24)
    c: Perpendicular(g43,g26)
    c: Coincident(g45,g33)
    c: Coincident(g45,g11)
    c: Coincident(g46,g32)
    c: Coincident(g46,g13)
    c: Perpendicular(g32,g46)
    c: Coincident(g47,g-8)
    c: Coincident(g47,g-7)
    c: Coincident(g48,g-8)
    c: Coincident(g48,g-7)
    c: Coincident(g50,g49)
    c: PointOnObject(g50,g48)
    c: Equal(g49,g50)
    c: Perpendicular(g49,g47)
    c: Perpendicular(g48,g50)
    c: Symmetric(g47,g47,g49)
    c: Coincident(g22,g49)
FEATURE [PartDesign::Pad] Pad006
  Direction = (-3e-16,2e-16,1)
  Length = 2.8
  Length2 = 10
  Placement = pos=(1.8e-14,-1.2e-14,-53) rot=(1,0,0;3.14159rad)
  Profile = -> Sketch006
  ReferenceAxis = -> Sketch006 [N_Axis]
  Type = 0
  expr: Length = Spreadsheet.acrylic_thin
FEATURE [PartDesign::Body] Body007  label="feet_right"
  Group = -> [Sketch006,Binder009,DatumPlane,Pad006]
  Origin = -> Origin009
  Tip = -> Pad006
COMPONENT P6 — recipe-attached ("cam_left_1", modeled in this document).
Construction recipe (the document's own serialized feature program — sketch geometry with constraints, then the solid features built on it; lengths are millimeters unless a unit is written):

FEATURE [PartDesign::FeatureBase] Clone
  BaseFeature = -> Body
FEATURE [PartDesign::Body] Body008  label="cam_left_1"
  Group = -> [Clone]
  Origin = -> Origin010
  Placement = pos=(0,0,0) rot=(0,1,0;3.14159rad)
  Tip = -> Clone
COMPONENT P7 — recipe-attached ("cam_left_2", modeled in this document).
Construction recipe (the document's own serialized feature program — sketch geometry with constraints, then the solid features built on it; lengths are millimeters unless a unit is written):

FEATURE [PartDesign::FeatureBase] Clone001
  BaseFeature = -> Body003
FEATURE [PartDesign::Body] Body009  label="cam_left_2"
  Group = -> [Clone001]
  Origin = -> Origin011
  Placement = pos=(0,0,0) rot=(0,1,0;3.14159rad)
  Tip = -> Clone001
COMPONENT P8 — recipe-attached ("cam_left_3", modeled in this document).
Construction recipe (the document's own serialized feature program — sketch geometry with constraints, then the solid features built on it; lengths are millimeters unless a unit is written):

FEATURE [PartDesign::FeatureBase] Clone002
  BaseFeature = -> Body004
FEATURE [PartDesign::Body] Body010  label="cam_left_3"
  Group = -> [Clone002]
  Origin = -> Origin012
  Placement = pos=(0,0,0) rot=(0,1,0;3.14159rad)
  Tip = -> Clone002
COMPONENT P9 — recipe-attached ("spacer_left", modeled in this document).
Construction recipe (the document's own serialized feature program — sketch geometry with constraints, then the solid features built on it; lengths are millimeters unless a unit is written):

FEATURE [PartDesign::FeatureBase] Clone003
  BaseFeature = -> Body005
FEATURE [PartDesign::Body] Body011  label="spacer_left"
  Group = -> [Clone003]
  Origin = -> Origin013
  Placement = pos=(0,0,0) rot=(0,1,0;3.14159rad)
  Tip = -> Clone003
COMPONENT P10 — recipe-attached ("leg_left", modeled in this document).
Construction recipe (the document's own serialized feature program — sketch geometry with constraints, then the solid features built on it; lengths are millimeters unless a unit is written):

FEATURE [PartDesign::FeatureBase] Clone006
  BaseFeature = -> Body002
FEATURE [PartDesign::Body] Body014  label="leg_left"
  Group = -> [Clone006]
  Origin = -> Origin016
  Placement = pos=(0,0,20) rot=(0,0,1;3.14159rad)
  Tip = -> Clone006
COMPONENT P11 — recipe-attached ("feet_left", modeled in this document).
Construction recipe (the document's own serialized feature program — sketch geometry with constraints, then the solid features built on it; lengths are millimeters unless a unit is written):

FEATURE [PartDesign::FeatureBase] Clone007
  BaseFeature = -> Body007
FEATURE [PartDesign::Body] Body015  label="feet_left"
  Group = -> [Clone007]
  Origin = -> Origin017
  Placement = pos=(1e-14,0,-83.2) rot=(0,1,0;3.14159rad)
  Tip = -> Clone007
COMPONENT P12 — recipe-attached ("body_right", modeled in this document).
Construction recipe (the document's own serialized feature program — sketch geometry with constraints, then the solid features built on it; lengths are millimeters unless a unit is written):

FEATURE [PartDesign::SubShapeBinder] Binder010
  BindCopyOnChange = 0
  BindMode = 0
  ClaimChildren = false
  Context = -> Body017 [Binder010.]
  Fuse = false
  MakeFace = true
  OffsetFill = false
  OffsetIntersection = false
  OffsetJoinType = 0
  OffsetOpenResult = false
  PartialLoad = false
  Relative = true
  Support = -> [Part001]
  _Version = 2
FEATURE [PartDesign::SubShapeBinder] Binder011
  BindCopyOnChange = 0
  BindMode = 0
  ClaimChildren = false
  Context = -> Body017 [Binder011.]
  Fuse = false
  MakeFace = true
  OffsetFill = false
  OffsetIntersection = false
  OffsetJoinType = 0
  OffsetOpenResult = false
  PartialLoad = false
  Relative = true
  Support = -> [Body002]
  _Version = 2
FEATURE [PartDesign::SubShapeBinder] Binder012
  BindCopyOnChange = 0
  BindMode = 0
  ClaimChildren = false
  Context = -> Body017 [Binder012.]
  Fuse = false
  MakeFace = true
  OffsetFill = false
  OffsetIntersection = false
  OffsetJoinType = 0
  OffsetOpenResult = false
  PartialLoad = false
  Relative = true
  Support = -> [Body014]
  _Version = 2
FEATURE [Sketcher::SketchObject] Sketch007
  ExternalGeometry = -> [Binder010,Binder011,Binder012]
  FullyConstrained = true
  MapMode = 5
  Placement = pos=(-9.4,0,0) rot=(0.57735,-0.57735,-0.57735;2.0944rad)
  Support = -> [Binder010]
  expr: Constraints[88] = Spreadsheet.acrylic_thin
  expr: Constraints[91] = Spreadsheet.acrylic_thin
  expr: Constraints[95] = Spreadsheet.acrylic_thin * 1.5
  sketch-geometry (42):
    g0: Circle CenterX=1.3e-15 CenterY=10.85 CenterZ=0 NormalX=0 NormalY=0 NormalZ=1 AngleXU=0 Radius=2.1
    g1: LineSegment StartX=8e-16 StartY=12.85 StartZ=0 EndX=8e-16 EndY=12.95 EndZ=0
    g2: Circle CenterX=-8.9 CenterY=20.85 CenterZ=0 NormalX=0 NormalY=0 NormalZ=1 AngleXU=0 Radius=1.55
    g3: Circle CenterX=8.9 CenterY=20.85 CenterZ=0 NormalX=0 NormalY=0 NormalZ=1 AngleXU=0 Radius=1.55
    g4: LineSegment StartX=2.83e-14 StartY=75 StartZ=0 EndX=-4e-14 EndY=70 EndZ=0
    g5: Circle CenterX=-5.8e-15 CenterY=72.5 CenterZ=0 NormalX=0 NormalY=0 NormalZ=1 AngleXU=0 Radius=1.55
    g6: ArcOfCircle CenterX=-8.15 CenterY=75.1 CenterZ=0 NormalX=0 NormalY=0 NormalZ=1 AngleXU=0 Radius=3 StartAngle=1.5708 EndAngle=3.14159
    g7: ArcOfCircle CenterX=8.15 CenterY=75.1 CenterZ=0 NormalX=0 NormalY=0 NormalZ=1 AngleXU=0 Radius=3 StartAngle=3e-16 EndAngle=1.5708
    g8: LineSegment StartX=11.15 StartY=75.1 StartZ=0 EndX=11.15 EndY=36.85 EndZ=0
    g9: ArcOfCircle CenterX=8.15 CenterY=9.85 CenterZ=0 NormalX=0 NormalY=0 NormalZ=1 AngleXU=0 Radius=3 StartAngle=4.71239 EndAngle=6.28319
    g10: LineSegment StartX=8.15 StartY=6.85 StartZ=0 EndX=-11.15 EndY=6.85 EndZ=0
    g11: LineSegment StartX=-11.15 StartY=39.85 StartZ=0 EndX=-11.15 EndY=75.1 EndZ=0
    g12: GeomPoint X=11.15 Y=6.85 Z=0
    g13: ArcOfCircle CenterX=-3.18082 CenterY=49.59 CenterZ=0 NormalX=0 NormalY=0 NormalZ=1 AngleXU=0 Radius=3 StartAngle=1.5708 EndAngle=3.14159
    g14: LineSegment StartX=-3.18082 StartY=52.59 StartZ=0 EndX=3.18082 EndY=52.59 EndZ=0
    g15: ArcOfCircle CenterX=3.18082 CenterY=49.59 CenterZ=0 NormalX=0 NormalY=0 NormalZ=1 AngleXU=0 Radius=3 StartAngle=0 EndAngle=1.5708
    g16: ArcOfCircle CenterX=3.18082 CenterY=28.85 CenterZ=0 NormalX=0 NormalY=0 NormalZ=1 AngleXU=0 Radius=3 StartAngle=4.71239 EndAngle=6.28319
    g17: LineSegment StartX=3.18082 StartY=25.85 StartZ=0 EndX=-3.18082 EndY=25.85 EndZ=0
    g18: ArcOfCircle CenterX=-3.18082 CenterY=28.85 CenterZ=0 NormalX=0 NormalY=0 NormalZ=1 AngleXU=0 Radius=3 StartAngle=3.14159 EndAngle=4.71239
    g19: LineSegment StartX=-6.18082 StartY=28.85 StartZ=0 EndX=-6.18082 EndY=49.59 EndZ=0
    g20: GeomPoint X=-6.18082 Y=52.59 Z=0
    g21: LineSegment StartX=6.18082 StartY=49.59 StartZ=0 EndX=6.18082 EndY=28.85 EndZ=0
    g22: LineSegment StartX=-11.15 StartY=6.85 StartZ=0 EndX=-37.15 EndY=6.85 EndZ=0
    g23: ArcOfCircle CenterX=-37.15 CenterY=7.85 CenterZ=0 NormalX=0 NormalY=0 NormalZ=1 AngleXU=0 Radius=1 StartAngle=3.14159 EndAngle=4.71239
    g24: ArcOfCircle CenterX=-39.15 CenterY=7.85 CenterZ=0 NormalX=0 NormalY=0 NormalZ=1 AngleXU=0 Radius=1 StartAngle=1e-16 EndAngle=3.14159
    g25: ArcOfCircle CenterX=-41.15 CenterY=7.85 CenterZ=0 NormalX=0 NormalY=0 NormalZ=1 AngleXU=0 Radius=1 StartAngle=3.14159 EndAngle=6.28319
    g26: LineSegment StartX=-42.15 StartY=7.85 StartZ=0 EndX=-42.15 EndY=35.85 EndZ=0
    g27: ArcOfCircle CenterX=-41.15 CenterY=35.85 CenterZ=0 NormalX=0 NormalY=0 NormalZ=1 AngleXU=0 Radius=1 StartAngle=2e-16 EndAngle=3.14159
    g28: ArcOfCircle CenterX=-39.15 CenterY=35.85 CenterZ=0 NormalX=0 NormalY=0 NormalZ=1 AngleXU=0 Radius=1 StartAngle=3.14159 EndAngle=6.28319
    g29: ArcOfCircle CenterX=-37.15 CenterY=35.85 CenterZ=0 NormalX=0 NormalY=0 NormalZ=1 AngleXU=0 Radius=1 StartAngle=1.5708 EndAngle=3.14159
    g30: LineSegment StartX=-37.15 StartY=36.85 StartZ=0 EndX=-14.15 EndY=36.85 EndZ=0
    g31: ArcOfCircle CenterX=-14.15 CenterY=39.85 CenterZ=0 NormalX=0 NormalY=0 NormalZ=1 AngleXU=0 Radius=3 StartAngle=4.71239 EndAngle=6.28319
    g32: LineSegment StartX=-8.15 StartY=78.1 StartZ=0 EndX=8.15 EndY=78.1 EndZ=0
    g33: ArcOfCircle CenterX=12.55 CenterY=12.45 CenterZ=0 NormalX=0 NormalY=0 NormalZ=1 AngleXU=0 Radius=1.4 StartAngle=2e-16 EndAngle=3.14159
    g34: LineSegment StartX=13.95 StartY=12.45 StartZ=0 EndX=13.95 EndY=8.25 EndZ=0
    g35: ArcOfCircle CenterX=15.35 CenterY=8.25 CenterZ=0 NormalX=0 NormalY=0 NormalZ=1 AngleXU=0 Radius=1.4 StartAngle=3.14159 EndAngle=6.28319
    g36: LineSegment StartX=16.75 StartY=8.25 StartZ=0 EndX=16.75 EndY=39.65 EndZ=0
    g37: ArcOfCircle CenterX=15.35 CenterY=39.65 CenterZ=0 NormalX=0 NormalY=0 NormalZ=1 AngleXU=0 Radius=1.4 StartAngle=-9e-16 EndAngle=3.14159
    g38: LineSegment StartX=13.95 StartY=39.65 StartZ=0 EndX=13.95 EndY=36.85 EndZ=0
    g39: LineSegment StartX=13.95 StartY=36.85 StartZ=0 EndX=11.15 EndY=36.85 EndZ=0
    g40: LineSegment StartX=8.15 StartY=6.85 StartZ=0 EndX=15.35 EndY=6.85 EndZ=0
    g41: LineSegment StartX=11.15 StartY=12.45 StartZ=0 EndX=11.15 EndY=9.85 EndZ=0
  constraints (105):
    c: PointOnObject(g1,g0)
    c: DistanceY(g1,g1) = 0.1
    c: Equal(g2,g3)
    c: Diameter(g2) = 3.1
    c: Diameter(g5) = 3.1
    c: Symmetric(g4,g4,g5)
    c: Tangent(g7,g8) = 1.5708
    c: Tangent(g9,g10) = 1.5708
    c: Tangent(g11,g6) = 1.5708
    c: Horizontal(g10)
    c: Vertical(g8)
    c: Vertical(g11)
    c: Equal(g6,g7)
    c: Equal(g7,g9)
    c: PointOnObject(g12,g8)
    c: PointOnObject(g12,g10)
    c: Distance(g0,g10) = 4
    c: Tangent(g13,g14) = 1.5708
    c: Tangent(g14,g15) = 1.5708
    c: Tangent(g16,g17) = 1.5708
    c: Tangent(g17,g18) = 1.5708
    c: Tangent(g19,g13) = 1.5708
    c: Horizontal(g14)
    c: Horizontal(g17)
    c: Vertical(g19)
    c: PointOnObject(g20,g14)
    c: PointOnObject(g20,g19)
    c: Radius(g13) = 3
    c: Coincident(g0,g-5)
    c: Coincident(g-5,g1)
    c: Perpendicular(g-5,g1)
    c: Coincident(g2,g-3)
    c: Coincident(g3,g-4)
    c: PointOnObject(g41,g-7)
    c: Coincident(g4,g-9)
    c: Coincident(g4,g-8)
    c: Tangent(g18,g19) = 1.5708
    c: Vertical(g21)
    c: Tangent(g21,g16) = 1.5708
    c: Tangent(g21,g15) = 1.5708
    c: Equal(g13,g15)
    c: Equal(g15,g16)
    c: Equal(g16,g18)
    c: PointOnObject(g18,g-10)
    c: PointOnObject(g16,g-11)
    c: Horizontal(g17,g-10)
    c: PointOnObject(g13,g-12)
    c: PointOnObject(g22,g-6)
    c: Horizontal(g22)
    c: Tangent(g22,g23) = 1.5708
    c: Tangent(g23,g24) = 1.5708
    c: Tangent(g24,g25) = 1.5708
    c: Vertical(g26)
    c: Tangent(g26,g27) = 1.5708
    c: Tangent(g27,g28) = 1.5708
    c: Tangent(g28,g29) = 1.5708
    c: Horizontal(g30)
    c: Coincident(g10,g22)
    c: Tangent(g11,g31) = -1.5708
    c: Tangent(g30,g31) = -1.5708
    c: Tangent(g29,g30) = 1.5708
    c: Tangent(g25,g26) = 1.5708
    c: Equal(g23,g24)
    c: Equal(g23,g25)
    c: Equal(g23,g27)
    c: Equal(g23,g28)
    c: Equal(g23,g29)
    c: Radius(g23) = 1
    c: Angle(g23) = 1.5708
    c: Angle(g24) = 3.14159
    c: Angle(g29) = 1.5708
    c: Angle(g28) = 3.14159
    c: Radius(g6) = 3
    c: Equal(g31,g6)
    c: DistanceY(g10,g30) = 30
    c: DistanceX(g22,g22) = 26
    c: Vertical(g11,g10)
    c: Horizontal(g32)
    c: Tangent(g32,g6) = 1.5708
    c: Tangent(g32,g7) = 1.5708
    c: Tangent(g32,g-8)
    c: Vertical(g34)
    c: Tangent(g34,g35) = -1.5708
    c: Vertical(g36)
    c: Vertical(g38)
    c: Coincident(g38,g39)
    c: Horizontal(g39)
    c: Equal(g39,g38)
    c: DistanceX(g39,g39) = 2.8
    c: Tangent(g36,g37) = -1.5708
    c: Tangent(g37,g38) = -1.5708
    c: Diameter(g37) = 2.8
    c: Equal(g35,g37)
    c: Tangent(g35,g36) = -1.5708
    c: Tangent(g33,g34) = 1.5708
    c: DistanceY(g35,g33) = 4.2
    c: Tangent(g33,g8) = -1.5708
    c: Coincident(g40,g9)
    c: Horizontal(g40)
    c: Horizontal(g39,g30)
    c: Tangent(g40,g35) = -1.5708
    c: Coincident(g8,g39)
    c: Vertical(g41)
    c: Coincident(g41,g33)
    c: Tangent(g41,g9) = 1.5708
FEATURE [PartDesign::Pad] Pad007
  Direction = (-1,2e-16,-2e-16)
  Length = 2.8
  Length2 = 10
  Profile = -> Sketch007
  ReferenceAxis = -> Sketch007 [N_Axis]
  Type = 0
  expr: Length = Spreadsheet.acrylic_thin
FEATURE [PartDesign::Body] Body017  label="body_right"
  Group = -> [Sketch007,Binder010,Binder011,Binder012,Pad007]
  Origin = -> Origin019
  Tip = -> Pad007
COMPONENT P13 — recipe-attached ("body_left", modeled in this document).
Construction recipe (the document's own serialized feature program — sketch geometry with constraints, then the solid features built on it; lengths are millimeters unless a unit is written):

FEATURE [PartDesign::FeatureBase] Clone008
  BaseFeature = -> Body017
FEATURE [PartDesign::Body] Body018  label="body_left"
  Group = -> [Clone008]
  Origin = -> Origin021
  Placement = pos=(21.6,0,0) rot=(0,0,1;0rad)
  Tip = -> Clone008
COMPONENT P14 — recipe-attached ("spacer_top_centre", modeled in this document).
Construction recipe (the document's own serialized feature program — sketch geometry with constraints, then the solid features built on it; lengths are millimeters unless a unit is written):

FEATURE [PartDesign::SubShapeBinder] Binder013
  BindCopyOnChange = 0
  BindMode = 0
  ClaimChildren = false
  Context = -> Body019 [Binder013.]
  Fuse = false
  MakeFace = true
  OffsetFill = false
  OffsetIntersection = false
  OffsetJoinType = 0
  OffsetOpenResult = false
  PartialLoad = false
  Relative = true
  Support = -> [Body017]
  _Version = 2
FEATURE [PartDesign::SubShapeBinder] Binder014
  BindCopyOnChange = 0
  BindMode = 0
  ClaimChildren = false
  Context = -> Body019 [Binder014.]
  Fuse = false
  MakeFace = true
  OffsetFill = false
  OffsetIntersection = false
  OffsetJoinType = 0
  OffsetOpenResult = false
  PartialLoad = false
  Relative = true
  Support = -> [Body018]
  _Version = 2
FEATURE [Sketcher::SketchObject] Sketch008
  ExternalGeometry = -> [Binder014]
  FullyConstrained = true
  MapMode = 5
  Placement = pos=(0,0,0) rot=(0.57735,0.57735,0.57735;2.0944rad)
  Support = -> [YZ_Plane020]
  sketch-geometry (2):
    g0: Circle CenterX=5e-16 CenterY=72.5 CenterZ=0 NormalX=0 NormalY=0 NormalZ=1 AngleXU=0 Radius=1.55
    g1: Circle CenterX=5e-16 CenterY=72.5 CenterZ=0 NormalX=0 NormalY=0 NormalZ=1 AngleXU=0 Radius=4
  constraints (4):
    c: Coincident(g0,g-3)
    c: Coincident(g1,g0)
    c: Equal(g0,g-3)
    c: Diameter(g1) = 8
FEATURE [PartDesign::Pad] Pad008
  Direction = (1,-2e-16,3e-16)
  Length = 18.8
  Length2 = 10
  Midplane = true
  Placement = pos=(0,0,0) rot=(0.57735,0.57735,0.57735;2.0944rad)
  Profile = -> Sketch008
  ReferenceAxis = -> Sketch008 [N_Axis]
  Type = 0
FEATURE [PartDesign::Body] Body019  label="spacer_top_centre"
  Group = -> [Sketch008,Binder013,Binder014,Pad008]
  Origin = -> Origin022
  Tip = -> Pad008
COMPONENT P15 — recipe-attached ("spacer_top_right", modeled in this document).
Construction recipe (the document's own serialized feature program — sketch geometry with constraints, then the solid features built on it; lengths are millimeters unless a unit is written):

FEATURE [PartDesign::SubShapeBinder] Binder015
  BindCopyOnChange = 0
  BindMode = 0
  ClaimChildren = false
  Context = -> Body020 [Binder015.]
  Fuse = false
  MakeFace = true
  OffsetFill = false
  OffsetIntersection = false
  OffsetJoinType = 0
  OffsetOpenResult = false
  PartialLoad = false
  Relative = true
  Support = -> [Body017]
  _Version = 2
FEATURE [PartDesign::SubShapeBinder] Binder016
  BindCopyOnChange = 0
  BindMode = 0
  ClaimChildren = false
  Context = -> Body020 [Binder016.]
  Fuse = false
  MakeFace = true
  OffsetFill = false
  OffsetIntersection = false
  OffsetJoinType = 0
  OffsetOpenResult = false
  PartialLoad = false
  Relative = true
  Support = -> [Body002]
  _Version = 2
FEATURE [Sketcher::SketchObject] Sketch009
  ExternalGeometry = -> [Binder015]
  FullyConstrained = true
  MapMode = 5
  Placement = pos=(-12.2,2.7e-15,-2.8e-15) rot=(-0.57735,0.57735,0.57735;4.18879rad)
  Support = -> [Binder015]
  sketch-geometry (2):
    g0: Circle CenterX=0 CenterY=72.5 CenterZ=0 NormalX=0 NormalY=0 NormalZ=1 AngleXU=0 Radius=1.55
    g1: Circle CenterX=0 CenterY=72.5 CenterZ=0 NormalX=0 NormalY=0 NormalZ=1 AngleXU=0 Radius=4
  constraints (4):
    c: Coincident(g0,g-3)
    c: Equal(g0,g-3)
    c: Coincident(g1,g0)
    c: Diameter(g1) = 8
FEATURE [PartDesign::Pad] Pad009
  Direction = (-1,2e-16,-2e-16)
  Length = 10
  Length2 = 10
  Profile = -> Sketch009
  ReferenceAxis = -> Sketch009 [N_Axis]
  Type = 3
  UpToFace = -> Binder016 [Face1]
FEATURE [Sketcher::SketchObject] Sketch010
  ExternalGeometry = -> [Pad009,Binder016]
  FullyConstrained = true
  MapMode = 5
  Placement = pos=(-24.3,-4.4e-15,-1.34e-14) rot=(0.57735,-0.57735,-0.57735;2.0944rad)
  Support = -> [Pad009]
  sketch-geometry (2):
    g0: Circle CenterX=-2.06e-14 CenterY=72.5 CenterZ=0 NormalX=0 NormalY=0 NormalZ=1 AngleXU=0 Radius=3
    g1: Circle CenterX=-2.06e-14 CenterY=72.5 CenterZ=0 NormalX=0 NormalY=0 NormalZ=1 AngleXU=0 Radius=1.55
  constraints (4):
    c: Equal(g1,g-6)
    c: Coincident(g0,g-6)
    c: Coincident(g0,g1)
    c: Diameter(g0) = 6
FEATURE [PartDesign::Pad] Pad010
  BaseFeature = -> Pad009
  Direction = (-1,-1e-16,-3e-16)
  Length = 6
  Length2 = 10
  Profile = -> Sketch010
  ReferenceAxis = -> Sketch010 [N_Axis]
  Type = 0
  expr: Length = Spreadsheet.acrylic_thin * 2 + 0.4
FEATURE [PartDesign::Body] Body020  label="spacer_top_right"
  Group = -> [Binder015,Binder016,Sketch009,Pad009,Sketch010,Pad010]
  Origin = -> Origin023
  Tip = -> Pad010
COMPONENT P16 — recipe-attached ("spacer_top_left", modeled in this document).
Construction recipe (the document's own serialized feature program — sketch geometry with constraints, then the solid features built on it; lengths are millimeters unless a unit is written):

FEATURE [PartDesign::FeatureBase] Clone009
  BaseFeature = -> Body020
FEATURE [PartDesign::Body] Body021  label="spacer_top_left"
  Group = -> [Clone009]
  Origin = -> Origin024
  Placement = pos=(0,0,0) rot=(0,0,1;3.14159rad)
  Tip = -> Clone009
COMPONENT P17 — recipe-attached ("trunk", modeled in this document).
Construction recipe (the document's own serialized feature program — sketch geometry with constraints, then the solid features built on it; lengths are millimeters unless a unit is written):

FEATURE [PartDesign::SubShapeBinder] Binder017
  BindCopyOnChange = 0
  BindMode = 0
  ClaimChildren = false
  Context = -> Body022 [Binder017.]
  Fuse = false
  MakeFace = true
  OffsetFill = false
  OffsetIntersection = false
  OffsetJoinType = 0
  OffsetOpenResult = false
  PartialLoad = false
  Relative = true
  Support = -> [Body017]
  _Version = 2
FEATURE [PartDesign::SubShapeBinder] Binder018
  BindCopyOnChange = 0
  BindMode = 0
  ClaimChildren = false
  Context = -> Body022 [Binder018.]
  Fuse = false
  MakeFace = true
  OffsetFill = false
  OffsetIntersection = false
  OffsetJoinType = 0
  OffsetOpenResult = false
  PartialLoad = false
  Relative = true
  Support = -> [Body018]
  _Version = 2
FEATURE [PartDesign::SubShapeBinder] Binder019
  BindCopyOnChange = 0
  BindMode = 0
  ClaimChildren = false
  Context = -> Body022 [Binder019.]
  Fuse = false
  MakeFace = true
  OffsetFill = false
  OffsetIntersection = false
  OffsetJoinType = 0
  OffsetOpenResult = false
  PartialLoad = false
  Relative = true
  Support = -> [Part001]
  _Version = 2
FEATURE [Sketcher::SketchObject] Sketch011
  ExternalGeometry = -> [Binder017,Binder018]
  FullyConstrained = true
  MapMode = 5
  Placement = pos=(0,-11.15,0) rot=(1,0,0;1.5708rad)
  Support = -> [Binder019]
  expr: Constraints[24] = Spreadsheet.acrylic_thin - 0.3
  expr: Constraints[25] = Spreadsheet.acrylic_thin + 0.3
  sketch-geometry (21):
    g0: LineSegment StartX=-9.4 StartY=36.85 StartZ=0 EndX=-12.2 EndY=36.85 EndZ=0
    g1: LineSegment StartX=-12.2 StartY=36.85 StartZ=0 EndX=-12.2 EndY=76.6 EndZ=0
    g2: ArcOfCircle CenterX=-10.7 CenterY=76.6 CenterZ=0 NormalX=0 NormalY=0 NormalZ=1 AngleXU=0 Radius=1.5 StartAngle=1.5708 EndAngle=3.14159
    g3: LineSegment StartX=-5 StartY=79.6 StartZ=0 EndX=-5 EndY=83.1 EndZ=0
    g4: ArcOfCircle CenterX=0 CenterY=89.345 CenterZ=0 NormalX=0 NormalY=0 NormalZ=1 AngleXU=0 Radius=8 StartAngle=5.38752 EndAngle=10.3204
    g5: LineSegment StartX=-9.4 StartY=36.85 StartZ=0 EndX=-9.4 EndY=9.95 EndZ=0
    g6: LineSegment StartX=-9.4 StartY=9.95 StartZ=0 EndX=-12.2 EndY=9.95 EndZ=0
    g7: LineSegment StartX=-12.2 StartY=9.95 StartZ=0 EndX=-12.2 EndY=6.85 EndZ=0
    g8: LineSegment StartX=-12.2 StartY=6.85 StartZ=0 EndX=0 EndY=6.85 EndZ=0
    g9: LineSegment StartX=-10.7 StartY=78.1 StartZ=0 EndX=-6.5 EndY=78.1 EndZ=0
    g10: ArcOfCircle CenterX=-6.5 CenterY=79.6 CenterZ=0 NormalX=0 NormalY=0 NormalZ=1 AngleXU=0 Radius=1.5 StartAngle=4.71239 EndAngle=6.28319
    g11: LineSegment StartX=12.2 StartY=9.95 StartZ=0 EndX=9.4 EndY=9.95 EndZ=0
    g12: LineSegment StartX=9.4 StartY=9.95 StartZ=0 EndX=9.4 EndY=36.85 EndZ=0
    g13: LineSegment StartX=9.4 StartY=36.85 StartZ=0 EndX=12.2 EndY=36.85 EndZ=0
    g14: LineSegment StartX=12.2 StartY=36.85 StartZ=0 EndX=12.2 EndY=76.6 EndZ=0
    g15: ArcOfCircle CenterX=10.7 CenterY=76.6 CenterZ=0 NormalX=0 NormalY=0 NormalZ=1 AngleXU=0 Radius=1.5 StartAngle=-4.4e-15 EndAngle=1.5708
    g16: LineSegment StartX=10.7 StartY=78.1 StartZ=0 EndX=6.5 EndY=78.1 EndZ=0
    g17: ArcOfCircle CenterX=6.5 CenterY=79.6 CenterZ=0 NormalX=0 NormalY=0 NormalZ=1 AngleXU=0 Radius=1.5 StartAngle=3.14159 EndAngle=4.71239
    g18: LineSegment StartX=5 StartY=79.6 StartZ=0 EndX=5 EndY=83.1 EndZ=0
    g19: LineSegment StartX=12.2 StartY=9.95 StartZ=0 EndX=12.2 EndY=6.85 EndZ=0
    g20: LineSegment StartX=12.2 StartY=6.85 StartZ=0 EndX=0 EndY=6.85 EndZ=0
  constraints (56):
    c: Coincident(g-3,g0)
    c: Coincident(g0,g-3)
    c: Coincident(g0,g1)
    c: Vertical(g1)
    c: Tangent(g1,g2) = 1.5708
    c: Vertical(g3)
    c: Coincident(g0,g5)
    c: Vertical(g5)
    c: Coincident(g5,g6)
    c: Horizontal(g6)
    c: Coincident(g6,g7)
    c: Vertical(g7)
    c: Coincident(g7,g8)
    c: Horizontal(g8)
    c: Radius(g2) = 1.5
    c: Angle(g2) = 1.5708
    c: Coincident(g4,g3)
    c: DistanceX(g-2,g3) = -5
    c: DistanceY(g3,g3) = 3.5
    c: Tangent(g2,g9) = 1.5708
    c: Tangent(g9,g10) = -1.5708
    c: Tangent(g10,g3) = -1.5708
    c: Equal(g10,g2)
    c: Equal(g0,g6)
    c: DistanceY(g6,g-5) = 2.5
    c: DistanceY(g7,g7) = 3.1
    c: PointOnObject(g8,g-2)
    c: Horizontal(g11)
    c: Coincident(g11,g12)
    c: Coincident(g12,g-4)
    c: Vertical(g12)
    c: Coincident(g12,g13)
    c: Coincident(g13,g-4)
    c: Coincident(g13,g14)
    c: Vertical(g14)
    c: Tangent(g14,g15) = -1.5708
    c: Horizontal(g16)
    c: Tangent(g16,g17) = 1.5708
    c: Vertical(g18)
    c: Tangent(g15,g16) = -1.5708
    c: Equal(g15,g17)
    c: Equal(g17,g2)
    c: Tangent(g17,g18) = 1.5708
    c: Equal(g14,g1)
    c: Equal(g16,g9)
    c: Equal(g12,g5)
    c: Equal(g11,g6)
    c: Coincident(g11,g19)
    c: Vertical(g19)
    c: Coincident(g19,g20)
    c: Coincident(g20,g8)
    c: Horizontal(g20)
    c: Coincident(g18,g4)
    c: PointOnObject(g4,g-2)
    c: Diameter(g4) = 16
    c: PointOnObject(g-9,g9)
FEATURE [PartDesign::Pad] Pad011
  Direction = (-2e-16,-1,2e-16)
  Length = 2.8
  Length2 = 10
  Profile = -> Sketch011
  ReferenceAxis = -> Sketch011 [N_Axis]
  Type = 0
  expr: Length = Spreadsheet.acrylic_thin
FEATURE [PartDesign::Body] Body022  label="trunk"
  Group = -> [Binder017,Binder018,Binder019,Sketch011,Pad011]
  Origin = -> Origin025
  Tip = -> Pad011
COMPONENT P18 — recipe-attached ("hand_right", modeled in this document).
Construction recipe (the document's own serialized feature program — sketch geometry with constraints, then the solid features built on it; lengths are millimeters unless a unit is written):

FEATURE [PartDesign::SubShapeBinder] Binder020
  BindCopyOnChange = 0
  BindMode = 0
  ClaimChildren = false
  Context = -> Body023 [Binder020.]
  Fuse = false
  MakeFace = true
  OffsetFill = false
  OffsetIntersection = false
  OffsetJoinType = 0
  OffsetOpenResult = false
  PartialLoad = false
  Relative = true
  Support = -> [Body020]
  _Version = 2
FEATURE [PartDesign::SubShapeBinder] Binder021
  BindCopyOnChange = 0
  BindMode = 0
  ClaimChildren = false
  Context = -> Body023 [Binder021.]
  Fuse = false
  MakeFace = true
  OffsetFill = false
  OffsetIntersection = false
  OffsetJoinType = 0
  OffsetOpenResult = false
  PartialLoad = false
  Relative = true
  Support = -> [Body002]
  _Version = 2
FEATURE [PartDesign::Plane] DatumPlane004
  AttachmentOffset = pos=(0,0,0.1) rot=(0,0,1;0rad)
  Length = 144.161
  MapMode = 5
  Placement = pos=(-27.2,7.1e-15,-1.5e-14) rot=(-0.57735,0.57735,0.57735;4.18879rad)
  ResizeMode = 0
  Support = -> [Binder021]
  Width = 139.673
FEATURE [Sketcher::SketchObject] Sketch012
  ExternalGeometry = -> [Binder020,Binder021]
  FullyConstrained = true
  MapMode = 5
  Placement = pos=(-27.2,7.1e-15,-1.5e-14) rot=(-0.57735,0.57735,0.57735;4.18879rad)
  Support = -> [DatumPlane004]
  expr: Constraints[39] = Spreadsheet.angle
  sketch-geometry (34):
    g0: LineSegment StartX=-37.8909 StartY=47.7513 StartZ=0 EndX=-5.65685 EndY=79.9853 EndZ=0
    g1: LineSegment StartX=5.65685 StartY=79.9853 StartZ=0 EndX=32.234 EndY=53.4081 EndZ=0
    g2: LineSegment StartX=36.4767 StartY=53.4081 StartZ=0 EndX=62.6396 EndY=79.5711 EndZ=0
    g3: LineSegment StartX=62.6396 StartY=79.5711 StartZ=0 EndX=69.7107 EndY=72.5 EndZ=0
    g4: LineSegment StartX=69.7107 StartY=72.5 StartZ=0 EndX=43.5477 EndY=46.337 EndZ=0
    g5: LineSegment StartX=25.163 StartY=46.337 StartZ=0 EndX=5 EndY=66.5 EndZ=0
    g6: LineSegment StartX=-5 StartY=66.5 StartZ=0 EndX=-30.8198 EndY=40.6802 EndZ=0
    g7: ArcOfCircle CenterX=-34.3553 CenterY=44.2157 CenterZ=0 NormalX=0 NormalY=0 NormalZ=1 AngleXU=0 Radius=5 StartAngle=2.35619 EndAngle=5.49779
    g8: ArcOfCircle CenterX=34.3553 CenterY=55.5294 CenterZ=0 NormalX=0 NormalY=0 NormalZ=1 AngleXU=0 Radius=3 StartAngle=3.92699 EndAngle=5.49779
    g9: LineSegment StartX=-37.8909 StartY=47.7513 StartZ=0 EndX=-30.8198 EndY=40.6802 EndZ=0
    g10: LineSegment StartX=-5 StartY=66.5 StartZ=0 EndX=5 EndY=66.5 EndZ=0
    g11: ArcOfCircle CenterX=34.3553 CenterY=55.5294 CenterZ=0 NormalX=0 NormalY=0 NormalZ=1 AngleXU=0 Radius=13 StartAngle=3.92699 EndAngle=5.49779
    g12: LineSegment StartX=-34.3553 StartY=44.2157 StartZ=0 EndX=-6.07107 EndY=72.5 EndZ=0
    g13: LineSegment StartX=6.07107 StartY=72.5 StartZ=0 EndX=34.3553 EndY=44.2157 EndZ=0
    g14: LineSegment StartX=34.3553 StartY=44.2157 StartZ=0 EndX=66.1751 EndY=76.0355 EndZ=0
    g15: LineSegment StartX=-6.07107 StartY=72.5 StartZ=0 EndX=6.07107 EndY=72.5 EndZ=0
    g16: LineSegment StartX=-2.11e-14 StartY=72.5 StartZ=0 EndX=-2.22e-14 EndY=66.5 EndZ=0
    g17: Circle CenterX=-2.11e-14 CenterY=72.5 CenterZ=0 NormalX=0 NormalY=0 NormalZ=1 AngleXU=0 Radius=3
    g18: ArcOfCircle CenterX=-2.36e-14 CenterY=74.3284 CenterZ=0 NormalX=0 NormalY=0 NormalZ=1 AngleXU=0 Radius=8 StartAngle=0.785398 EndAngle=2.35619
    g19: LineSegment StartX=74.092 StartY=76.6039 StartZ=0 EndX=78.3347 EndY=80.8466 EndZ=0
    g20: LineSegment StartX=78.3347 StartY=80.8466 StartZ=0 EndX=76.7817 EndY=86.6421 EndZ=0
    g21: LineSegment StartX=76.7817 StartY=86.6421 StartZ=0 EndX=70.9862 EndY=88.195 EndZ=0
    g22: LineSegment StartX=70.9862 StartY=88.195 StartZ=0 EndX=66.7436 EndY=83.9524 EndZ=0
    g23: LineSegment StartX=66.7436 StartY=83.9524 StartZ=0 EndX=68.2965 EndY=78.1569 EndZ=0
    g24: LineSegment StartX=68.2965 StartY=78.1569 StartZ=0 EndX=74.092 EndY=76.6039 EndZ=0
    g25: Circle CenterX=72.5391 CenterY=82.3995 CenterZ=0 NormalX=0 NormalY=0 NormalZ=1 AngleXU=0 Radius=6
    g26: LineSegment StartX=66.1751 StartY=76.0355 StartZ=0 EndX=68.2965 EndY=78.1569 EndZ=0
    g27: LineSegment StartX=70.9862 StartY=88.195 StartZ=0 EndX=68.1578 EndY=91.0235 EndZ=0
    g28: LineSegment StartX=68.1578 StartY=91.0235 StartZ=0 EndX=61.3856 EndY=84.2513 EndZ=0
    g29: LineSegment StartX=61.3856 StartY=84.2513 StartZ=0 EndX=62.6396 EndY=79.5711 EndZ=0
    g30: LineSegment StartX=69.7107 StartY=72.5 StartZ=0 EndX=74.3909 EndY=71.2459 EndZ=0
    g31: LineSegment StartX=74.3909 StartY=71.2459 StartZ=0 EndX=81.1631 EndY=78.0182 EndZ=0
    g32: LineSegment StartX=81.1631 StartY=78.0182 StartZ=0 EndX=78.3347 EndY=80.8466 EndZ=0
    g33: Circle CenterX=-34.3553 CenterY=44.2157 CenterZ=0 NormalX=0 NormalY=0 NormalZ=1 AngleXU=0 Radius=0.6
  constraints (84):
    c: Coincident(g2,g3)
    c: Coincident(g3,g4)
    c: Tangent(g6,g7) = 1.5708
    c: Tangent(g1,g8) = -1.5708
    c: Tangent(g2,g8) = -1.5708
    c: Perpendicular(g2,g3)
    c: Perpendicular(g4,g3)
    c: Perpendicular(g5,g4)
    c: Perpendicular(g2,g1)
    c: Tangent(g7,g0) = 1.5708
    c: Perpendicular(g5,g6)
    c: Angle(g7) = 3.14159
    c: Coincident(g9,g0)
    c: Coincident(g9,g6)
    c: Distance(g9) = 10
    c: Coincident(g10,g6)
    c: Coincident(g10,g5)
    c: Tangent(g11,g5) = 1.5708
    c: Tangent(g11,g4) = 1.5708
    c: Coincident(g11,g8)
    c: Symmetric(g2,g3,g14)
    c: Perpendicular(g14,g3)
    c: Coincident(g14,g13)
    c: Distance(g14) = 45
    c: Perpendicular(g13,g14)
    c: Perpendicular(g12,g13)
    c: Coincident(g12,g7)
    c: Angle(g10,g5) = 2.35619
    c: Coincident(g12,g15)
    c: Coincident(g13,g15)
    c: Perpendicular(g16,g10)
    c: Perpendicular(g16,g15)
    c: Symmetric(g6,g5,g16)
    c: Symmetric(g12,g13,g16)
    c: Coincident(g16,g-3)
    c: Equal(g12,g13)
    c: Distance(g12) = 40
    c: Coincident(g17,g16)
    c: Equal(g17,g-3)
    c: Angle(g16) = 4.71239
    c: Tangent(g18,g1) = 1.5708
    c: Tangent(g18,g0) = 1.5708
    c: Equal(g3,g9)
    c: Coincident(g19,g20)
    c: Coincident(g20,g21)
    c: Coincident(g21,g22)
    c: Coincident(g22,g23)
    c: Coincident(g23,g24)
    c: Coincident(g24,g19)
    c: Equal(g19, g20-g24) x5
    c: PointOnObject(g19,g25)
    c: PointOnObject(g20,g25)
    c: PointOnObject(g21,g25)
    c: PointOnObject(g22,g25)
    c: PointOnObject(g23,g25)
    c: PointOnObject(g24,g25)
    c: Parallel(g22,g14)
    c: Coincident(g26,g14)
    c: Coincident(g26,g23)
    c: Perpendicular(g3,g26)
    c: Distance(g23) = 6
    c: Distance(g26) = 3
    c: Coincident(g22,g27)
    c: Coincident(g27,g28)
    c: Coincident(g28,g29)
    c: Coincident(g29,g2)
    c: Coincident(g4,g30)
    c: Coincident(g30,g31)
    c: Coincident(g31,g32)
    c: Coincident(g32,g19)
    c: Equal(g27,g32)
    c: Perpendicular(g22,g27)
    c: Perpendicular(g32,g19)
    c: Distance(g27) = 4
    c: Perpendicular(g28,g27)
    c: Perpendicular(g31,g32)
    c: Parallel(g24,g30)
    c: Parallel(g29,g23)
    c: Distance(g10) = 10
    c: Distance(g16) = 6
    c: Radius(g18) = 8
    c: Radius(g8) = 3
    c: Coincident(g33,g7)
    c: Diameter(g33) = 1.2
FEATURE [PartDesign::Pad] Pad012
  Direction = (-1,0,-4e-16)
  Length = 2.8
  Length2 = 10
  Placement = pos=(-27.2,-5e-15,-1.5e-14) rot=(0.57735,-0.57735,-0.57735;2.0944rad)
  Profile = -> Sketch012
  ReferenceAxis = -> Sketch012 [N_Axis]
  Type = 0
  expr: Length = Spreadsheet.acrylic_thin
FEATURE [PartDesign::Body] Body023  label="hand_right"
  Group = -> [Binder020,Binder021,DatumPlane004,Sketch012,Pad012]
  Origin = -> Origin026
  Tip = -> Pad012
COMPONENT P19 — recipe-attached ("hand_left", modeled in this document).
Construction recipe (the document's own serialized feature program — sketch geometry with constraints, then the solid features built on it; lengths are millimeters unless a unit is written):

FEATURE [PartDesign::FeatureBase] Clone010
  BaseFeature = -> Body023
FEATURE [PartDesign::Body] Body024  label="hand_left"
  Group = -> [Clone010]
  Origin = -> Origin027
  Placement = pos=(57.2,51.26,21.23) rot=(1,0,0;0.785398rad)
  Tip = -> Clone010
COMPONENT P20 — recipe-attached ("Body", modeled in this document).
Construction recipe (the document's own serialized feature program — sketch geometry with constraints, then the solid features built on it; lengths are millimeters unless a unit is written):

FEATURE [Sketcher::SketchObject] Sketch013
  FullyConstrained = true
  MapMode = 5
  Support = -> [XY_Plane026]
  sketch-geometry (4):
    g0: LineSegment StartX=-12 StartY=12 StartZ=0 EndX=12 EndY=12 EndZ=0
    g1: LineSegment StartX=12 StartY=12 StartZ=0 EndX=12 EndY=-12 EndZ=0
    g2: LineSegment StartX=12 StartY=-12 StartZ=0 EndX=-12 EndY=-12 EndZ=0
    g3: LineSegment StartX=-12 StartY=-12 StartZ=0 EndX=-12 EndY=12 EndZ=0
  constraints (11):
    c: Coincident(g0,g1)
    c: Coincident(g1,g2)
    c: Coincident(g2,g3)
    c: Coincident(g3,g0)
    c: Horizontal(g0)
    c: Horizontal(g2)
    c: Vertical(g1)
    c: Vertical(g3)
    c: Symmetric(g1,g0,g-1)
    c: Equal(g0,g3)
    c: DistanceX(g0,g0) = 24
FEATURE [PartDesign::Pad] Pad013
  Direction = (0,0,1)
  Length = 10
  Length2 = 10
  Profile = -> Sketch013
  ReferenceAxis = -> Sketch013 [N_Axis]
  Reversed = true
  Type = 0
FEATURE [PartDesign::Body] Body025  label="Body"
  Group = -> [Sketch013,Pad013]
  Origin = -> Origin028
  Tip = -> Pad013
COMPONENT P21 — geometry summary ("Motor"; no construction recipe available for this part):
  bounding box: 70.3 x 36.8 x 22.5 mm
  tessellated surface: 28,976 triangles
  volume: 23502 mm^3 (40% of its bounding box)
  symmetry: mirror-symmetric across its y mid-plane
COMPONENT P22 — geometry summary ("batt_9V005_cp_sp011"; no construction recipe available for this part):
  bounding box: 26.3 x 13.6 x 5.4 mm
  tessellated surface: 34,436 triangles
  volume: 19375 mm^3 (1008% of its bounding box)
PROVENANCE & LICENSES
A FreeCAD (.FCStd) document from a public repository crawl; recipes are the document's own serialized feature recipes (and, for linked parts, companion documents' recipes).
License: gpl-3.0.
